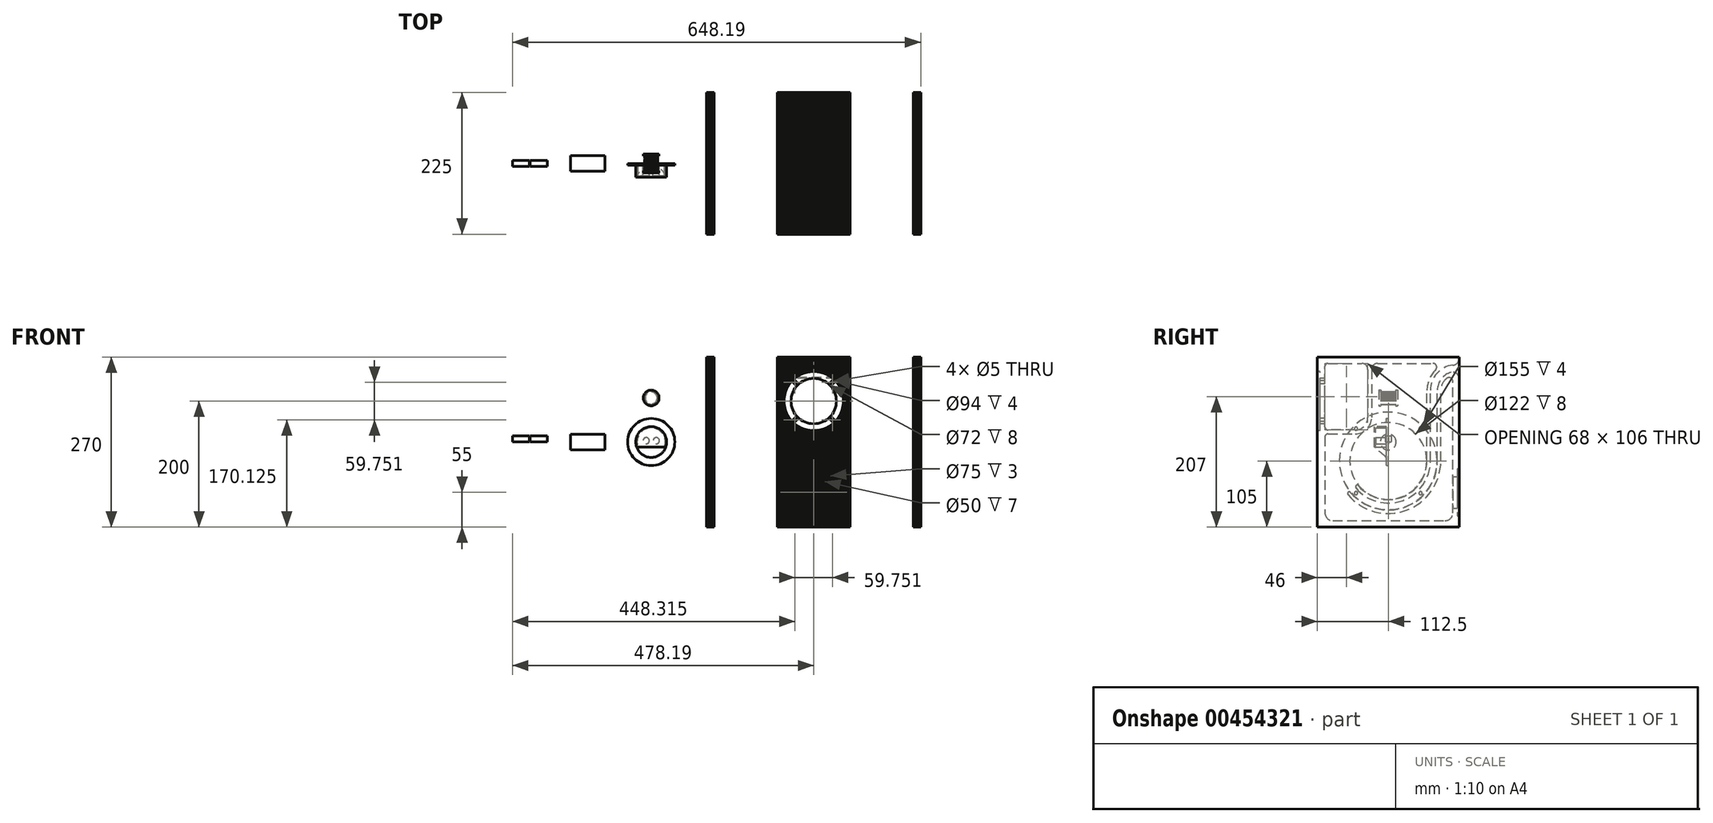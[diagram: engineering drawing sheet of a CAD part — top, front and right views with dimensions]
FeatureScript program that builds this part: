
annotation { "Feature Type Name" : "Feature", "Feature Type Description" : "" }
export const myFeature = defineFeature(function(context is Context, id is Id, definition is map)
    precondition{}
    {
        {
            var Q0;
            Q0=qCreatedBy(makeId("Right.planeOp"),FACE);
            var sketch = newSketch(context, id + "F0", { "sketchPlane" : qUnion([Q0])});
            skLineSegment(sketch, "E0", {"start": v(255.52, -132.38) * mm, "end": v(480.52, -132.38) * mm, "construction": true});
            skLineSegment(sketch, "E1", {"start": v(480.52, -132.38) * mm, "end": v(480.52, 137.62) * mm, "construction": true});
            skSolve(sketch);
        }
        {
            var Q0;
            Q0=qCreatedBy(makeId("Right.planeOp"),FACE);
            var sketch = newSketch(context, id + "F1", { "sketchPlane" : qUnion([Q0])});
            skPoint(sketch, "E2.middle", {"position": v(0, 0) * mm});
            skArc(sketch, "E3.MirrorCS", {"start": v(-88, -125) * mm, "mid": v(-96.84, -121.34) * mm, "end": v(-100.5, -112.5) * mm});
            skArc(sketch, "E4.MirrorCS", {"start": v(-95.5, 19) * mm, "mid": v(-99.04, 20.46) * mm, "end": v(-100.5, 24) * mm});
            skLineSegment(sketch, "E5", {"start": v(-100.5, 24) * mm, "end": v(-100.5, 120) * mm});
            skArc(sketch, "E6", {"start": v(-95.5, 125) * mm, "mid": v(-99.04, 123.54) * mm, "end": v(-100.5, 120) * mm});
            skLineSegment(sketch, "E7", {"start": v(-95.5, 125) * mm, "end": v(-42.5, 125) * mm});
            skArc(sketch, "E8", {"start": v(-32.5, 115) * mm, "mid": v(-35.43, 122.07) * mm, "end": v(-42.5, 125) * mm});
            skLineSegment(sketch, "E9", {"start": v(-32.5, 115) * mm, "end": v(-32.5, 39) * mm});
            skArc(sketch, "E10", {"start": v(-52.5, 19) * mm, "mid": v(-38.36, 24.86) * mm, "end": v(-32.5, 39) * mm});
            skLineSegment(sketch, "E11", {"start": v(-52.5, 19) * mm, "end": v(-95.5, 19) * mm});
            skLineSegment(sketch, "E12", {"start": v(-95.5, 13) * mm, "end": v(-52.5, 13) * mm});
            skLineSegment(sketch, "E13", {"start": v(-26.5, 115) * mm, "end": v(-26.5, 39) * mm});
            skArc(sketch, "E14", {"start": v(-52.5, 13) * mm, "mid": v(-34.12, 20.62) * mm, "end": v(-26.5, 39) * mm});
            skArc(sketch, "E15", {"start": v(-16.5, 125) * mm, "mid": v(-23.57, 122.07) * mm, "end": v(-26.5, 115) * mm});
            skArc(sketch, "E16", {"start": v(-95.5, 13) * mm, "mid": v(-99.04, 11.54) * mm, "end": v(-100.5, 8) * mm});
            skLineSegment(sketch, "E17", {"start": v(-100.5, 8) * mm, "end": v(-100.5, -112.5) * mm});
            skLineSegment(sketch, "E18", {"start": v(-88, -125) * mm, "end": v(90, -125) * mm});
            skArc(sketch, "E19", {"start": v(90, -125) * mm, "mid": v(98.84, -121.34) * mm, "end": v(102.5, -112.5) * mm});
            skLineSegment(sketch, "E20", {"start": v(102.5, -112.5) * mm, "end": v(102.5, 96.26) * mm});
            skLineSegment(sketch, "E21", {"start": v(-16.5, 125) * mm, "end": v(70.97, 125) * mm});
            skArc(sketch, "E22", {"start": v(75.35, 114.9) * mm, "mid": v(76.47, 121.39) * mm, "end": v(70.97, 125) * mm});
            skArc(sketch, "E23", {"start": v(112.5, 100.85) * mm, "mid": v(108.7, 108.7) * mm, "end": v(100.2, 110.58) * mm});
            skLineSegment(sketch, "E24", {"start": v(0, -30) * mm, "end": v(-76.6, -94.28) * mm, "construction": true});
            skArc(sketch, "E25", {"start": v(67, -30) * mm, "mid": v(22.92, -92.96) * mm, "end": v(-51.32, -73.07) * mm});
            skArc(sketch, "E26", {"start": v(102.5, 122.2) * mm, "mid": v(109.57, 125.12) * mm, "end": v(112.5, 132.2) * mm});
            skArc(sketch, "E27", {"start": v(78, -30) * mm, "mid": v(26.68, -103.3) * mm, "end": v(-59.75, -80.14) * mm});
            skArc(sketch, "E28", {"start": v(102.5, 96.26) * mm, "mid": v(99.32, 101.55) * mm, "end": v(93.16, 101.24) * mm});
            skLineSegment(sketch, "E29.bottom", {"start": v(-112.5, 135) * mm, "end": v(112.5, 135) * mm});
            skLineSegment(sketch, "E29.top", {"start": v(-112.5, -135) * mm, "end": v(112.5, -135) * mm});
            skLineSegment(sketch, "E29.left", {"start": v(-112.5, 135) * mm, "end": v(-112.5, -135) * mm});
            skLineSegment(sketch, "E30", {"start": v(112.5, 100.85) * mm, "end": v(112.5, -135) * mm});
            skArc(sketch, "E31", {"start": v(67, 82) * mm, "mid": v(77.15, 108.81) * mm, "end": v(102.5, 122.2) * mm});
            skLineSegment(sketch, "E32", {"start": v(112.5, 135) * mm, "end": v(112.5, 132.2) * mm});
            skArc(sketch, "E33", {"start": v(78, 82) * mm, "mid": v(84.2, 100.1) * mm, "end": v(100.2, 110.58) * mm});
            skArc(sketch, "E34", {"start": v(61.5, -30) * mm, "mid": v(21.03, -87.8) * mm, "end": v(-47.11, -69.53) * mm});
            skArc(sketch, "E35", {"start": v(83.5, -30) * mm, "mid": v(28.56, -108.46) * mm, "end": v(-63.96, -83.67) * mm});
            skArc(sketch, "E36", {"start": v(-59.75, -80.14) * mm, "mid": v(-63.63, -79.8) * mm, "end": v(-63.96, -83.67) * mm});
            skArc(sketch, "E37", {"start": v(-47.11, -69.53) * mm, "mid": v(-50.99, -69.2) * mm, "end": v(-51.32, -73.07) * mm});
            skLineSegment(sketch, "E38", {"start": v(67, -30) * mm, "end": v(67, 82) * mm});
            skLineSegment(sketch, "E39", {"start": v(78, -30) * mm, "end": v(78, 82) * mm});
            skLineSegment(sketch, "E40", {"start": v(61.5, -30) * mm, "end": v(61.5, 82) * mm});
            skArc(sketch, "E41", {"start": v(61.5, 82) * mm, "mid": v(65.1, 99.85) * mm, "end": v(75.35, 114.9) * mm});
            skLineSegment(sketch, "E42", {"start": v(83.5, -30) * mm, "end": v(83.5, 82) * mm});
            skArc(sketch, "E43", {"start": v(83.5, 82) * mm, "mid": v(86.05, 92.76) * mm, "end": v(93.16, 101.24) * mm});
            skSolve(sketch);
        }
        {
            var Q0;
            Q0 = qSketchRegion(id + "F1", true);
            extrude(context, id + "F2", {"entities" : qUnion([Q0]), "depth" : 116 * mm, "offsetDistance" : 25 * mm});
        }
        {
            var Q0;
            Q0=qCreatedBy(makeId("Top.planeOp"),FACE);
            var sketch = newSketch(context, id + "F3", { "sketchPlane" : qUnion([Q0])});
            skLineSegment(sketch, "E44.bottom", {"start": v(-112, 112.5) * mm, "end": v(-100, 112.5) * mm});
            skLineSegment(sketch, "E44.top", {"start": v(-112, -112.5) * mm, "end": v(-100, -112.5) * mm});
            skLineSegment(sketch, "E44.left", {"start": v(-112, 112.5) * mm, "end": v(-112, -112.5) * mm});
            skLineSegment(sketch, "E44.right", {"start": v(-100, 112.5) * mm, "end": v(-100, -112.5) * mm});
            skPoint(sketch, "E44.middle", {"position": v(-106, 0) * mm});
            skSolve(sketch);
        }
        {
            var Q0;
            Q0 = qSketchRegion(id + "F3", true);
            extrude(context, id + "F4", {"entities" : qUnion([Q0]), "depth" : 270 * mm, "offsetDistance" : 25 * mm, "symmetric" : true});
        }
        {
            var Q0;
            Q0=makeQuery(id+"F4.opExtrude","SWEPT_FACE",FACE,{"disambiguationData":[OSD([sQuery(id+"F3.wireOp",EDGE,"E44.left")])]});
            var sketch = newSketch(context, id + "F5", { "sketchPlane" : qUnion([Q0])});
            skCircle(sketch, "E45", {"center": v(0, -30) * mm, "radius": 77.5 * mm});
            skPoint(sketch, "E45.centerSnap0", {"position": v(0, -135) * mm});
            skSolve(sketch);
        }
        {
            var Q0;
            Q0 = qSketchRegion(id + "F5", true);
            extrude(context, id + "F6", {"entities" : qUnion([Q0]), "operationType" : NewBodyOperationType.REMOVE, "oppositeDirection" : true, "depth" : 4 * mm, "offsetDistance" : 25 * mm});
        }
        {
            var Q0;
            Q0=makeQuery(id+"F6.boolean.opBoolean","COPY",FACE,{"derivedFrom":makeQuery(id+"F6.opExtrude","CAP_FACE",FACE,{"disambiguationData":[OSD([sQuery(id+"F5.wireOp",EDGE,"E45")])],"isStart":false})});
            var sketch = newSketch(context, id + "F7", { "sketchPlane" : qUnion([Q0])});
            skCircle(sketch, "E46", {"center": v(0, -30) * mm, "radius": 61 * mm});
            skSolve(sketch);
        }
        {
            var Q0;
            Q0 = qSketchRegion(id + "F7", true);
            extrude(context, id + "F8", {"entities" : qUnion([Q0]), "operationType" : NewBodyOperationType.REMOVE, "oppositeDirection" : true, "depth" : 8 * mm, "offsetDistance" : 25 * mm});
        }
        {
            var Q0;
            Q0=qCreatedBy(makeId("Top.planeOp"),FACE);
            var sketch = newSketch(context, id + "F9", { "sketchPlane" : qUnion([Q0])});
            skLineSegment(sketch, "E47.bottom", {"start": v(228, 112.5) * mm, "end": v(216, 112.5) * mm});
            skLineSegment(sketch, "E47.top", {"start": v(228, -112.5) * mm, "end": v(216, -112.5) * mm});
            skLineSegment(sketch, "E47.left", {"start": v(228, 112.5) * mm, "end": v(228, -112.5) * mm});
            skLineSegment(sketch, "E47.right", {"start": v(216, 112.5) * mm, "end": v(216, -112.5) * mm});
            skPoint(sketch, "E47.middle", {"position": v(222, 0) * mm});
            skSolve(sketch);
        }
        {
            var Q0;
            Q0 = qSketchRegion(id + "F9", true);
            extrude(context, id + "F10", {"entities" : qUnion([Q0]), "depth" : 270 * mm, "offsetDistance" : 25 * mm, "symmetric" : true});
        }
        {
            var Q0;
            Q0=makeQuery(id+"F2.opExtrude","SWEPT_FACE",FACE,{"disambiguationData":[OSD([sQuery(id+"F1.wireOp",EDGE,"E29.left")])]});
            var sketch = newSketch(context, id + "F11", { "sketchPlane" : qUnion([Q0])});
            skCircle(sketch, "E48", {"center": v(58, 65) * mm, "radius": 47 * mm});
            skPoint(sketch, "E48.centerSnap0", {"position": v(58, 135) * mm});
            skSolve(sketch);
        }
        {
            var Q0;
            Q0 = qSketchRegion(id + "F11", true);
            extrude(context, id + "F12", {"entities" : qUnion([Q0]), "operationType" : NewBodyOperationType.REMOVE, "oppositeDirection" : true, "depth" : 4 * mm, "offsetDistance" : 25 * mm});
        }
        {
            var Q0;
            Q0=makeQuery(id+"F12.boolean.opBoolean","COPY",FACE,{"derivedFrom":makeQuery(id+"F12.opExtrude","CAP_FACE",FACE,{"disambiguationData":[OSD([sQuery(id+"F11.wireOp",EDGE,"E48")])],"isStart":false})});
            var sketch = newSketch(context, id + "F13", { "sketchPlane" : qUnion([Q0])});
            skCircle(sketch, "E49", {"center": v(58, 65) * mm, "radius": 36 * mm});
            skSolve(sketch);
        }
        {
            var Q0;
            Q0 = qSketchRegion(id + "F13", true);
            extrude(context, id + "F14", {"entities" : qUnion([Q0]), "operationType" : NewBodyOperationType.REMOVE, "oppositeDirection" : true, "depth" : 8 * mm, "offsetDistance" : 25 * mm});
        }
        {
            var Q0;
            Q0=makeQuery(id+"F2.opExtrude","SWEPT_FACE",FACE,{"disambiguationData":[OSD([sQuery(id+"F1.wireOp",EDGE,"E29.left")])]});
            var sketch = newSketch(context, id + "F15", { "sketchPlane" : qUnion([Q0])});
            skLineSegment(sketch, "E50.bottom", {"start": v(224, -150) * mm, "end": v(226, -150) * mm});
            skLineSegment(sketch, "E50.top", {"start": v(224, 150) * mm, "end": v(226, 150) * mm});
            skLineSegment(sketch, "E50.left", {"start": v(224, -150) * mm, "end": v(224, 150) * mm});
            skLineSegment(sketch, "E50.right", {"start": v(226, -150) * mm, "end": v(226, 150) * mm});
            skPoint(sketch, "E50.middle", {"position": v(225, 0) * mm});
            skLineSegment(sketch, "E51.1.0.0", {"start": v(220, 150) * mm, "end": v(222, 150) * mm});
            skLineSegment(sketch, "E51.1.0.1", {"start": v(220, -150) * mm, "end": v(220, 150) * mm});
            skLineSegment(sketch, "E51.1.0.2", {"start": v(222, -150) * mm, "end": v(222, 150) * mm});
            skLineSegment(sketch, "E51.1.0.3", {"start": v(220, -150) * mm, "end": v(222, -150) * mm});
            skLineSegment(sketch, "E51.2.0.0", {"start": v(216, 150) * mm, "end": v(218, 150) * mm});
            skLineSegment(sketch, "E51.2.0.1", {"start": v(216, -150) * mm, "end": v(216, 150) * mm});
            skLineSegment(sketch, "E51.2.0.2", {"start": v(218, -150) * mm, "end": v(218, 150) * mm});
            skLineSegment(sketch, "E51.2.0.3", {"start": v(216, -150) * mm, "end": v(218, -150) * mm});
            skLineSegment(sketch, "E51.3.0.0", {"start": v(212, 150) * mm, "end": v(214, 150) * mm});
            skLineSegment(sketch, "E51.3.0.1", {"start": v(212, -150) * mm, "end": v(212, 150) * mm});
            skLineSegment(sketch, "E51.3.0.2", {"start": v(214, -150) * mm, "end": v(214, 150) * mm});
            skLineSegment(sketch, "E51.3.0.3", {"start": v(212, -150) * mm, "end": v(214, -150) * mm});
            skLineSegment(sketch, "E51.4.0.0", {"start": v(208, 150) * mm, "end": v(210, 150) * mm});
            skLineSegment(sketch, "E51.4.0.1", {"start": v(208, -150) * mm, "end": v(208, 150) * mm});
            skLineSegment(sketch, "E51.4.0.2", {"start": v(210, -150) * mm, "end": v(210, 150) * mm});
            skLineSegment(sketch, "E51.4.0.3", {"start": v(208, -150) * mm, "end": v(210, -150) * mm});
            skLineSegment(sketch, "E51.5.0.0", {"start": v(204, 150) * mm, "end": v(206, 150) * mm});
            skLineSegment(sketch, "E51.5.0.1", {"start": v(204, -150) * mm, "end": v(204, 150) * mm});
            skLineSegment(sketch, "E51.5.0.2", {"start": v(206, -150) * mm, "end": v(206, 150) * mm});
            skLineSegment(sketch, "E51.5.0.3", {"start": v(204, -150) * mm, "end": v(206, -150) * mm});
            skLineSegment(sketch, "E51.6.0.0", {"start": v(200, 150) * mm, "end": v(202, 150) * mm});
            skLineSegment(sketch, "E51.6.0.1", {"start": v(200, -150) * mm, "end": v(200, 150) * mm});
            skLineSegment(sketch, "E51.6.0.2", {"start": v(202, -150) * mm, "end": v(202, 150) * mm});
            skLineSegment(sketch, "E51.6.0.3", {"start": v(200, -150) * mm, "end": v(202, -150) * mm});
            skLineSegment(sketch, "E51.7.0.0", {"start": v(196, 150) * mm, "end": v(198, 150) * mm});
            skLineSegment(sketch, "E51.7.0.1", {"start": v(196, -150) * mm, "end": v(196, 150) * mm});
            skLineSegment(sketch, "E51.7.0.2", {"start": v(198, -150) * mm, "end": v(198, 150) * mm});
            skLineSegment(sketch, "E51.7.0.3", {"start": v(196, -150) * mm, "end": v(198, -150) * mm});
            skLineSegment(sketch, "E51.8.0.0", {"start": v(192, 150) * mm, "end": v(194, 150) * mm});
            skLineSegment(sketch, "E51.8.0.1", {"start": v(192, -150) * mm, "end": v(192, 150) * mm});
            skLineSegment(sketch, "E51.8.0.2", {"start": v(194, -150) * mm, "end": v(194, 150) * mm});
            skLineSegment(sketch, "E51.8.0.3", {"start": v(192, -150) * mm, "end": v(194, -150) * mm});
            skLineSegment(sketch, "E51.9.0.0", {"start": v(188, 150) * mm, "end": v(190, 150) * mm});
            skLineSegment(sketch, "E51.9.0.1", {"start": v(188, -150) * mm, "end": v(188, 150) * mm});
            skLineSegment(sketch, "E51.9.0.2", {"start": v(190, -150) * mm, "end": v(190, 150) * mm});
            skLineSegment(sketch, "E51.9.0.3", {"start": v(188, -150) * mm, "end": v(190, -150) * mm});
            skLineSegment(sketch, "E51.10.0.0", {"start": v(184, 150) * mm, "end": v(186, 150) * mm});
            skLineSegment(sketch, "E51.10.0.1", {"start": v(184, -150) * mm, "end": v(184, 150) * mm});
            skLineSegment(sketch, "E51.10.0.2", {"start": v(186, -150) * mm, "end": v(186, 150) * mm});
            skLineSegment(sketch, "E51.10.0.3", {"start": v(184, -150) * mm, "end": v(186, -150) * mm});
            skLineSegment(sketch, "E51.11.0.0", {"start": v(180, 150) * mm, "end": v(182, 150) * mm});
            skLineSegment(sketch, "E51.11.0.1", {"start": v(180, -150) * mm, "end": v(180, 150) * mm});
            skLineSegment(sketch, "E51.11.0.2", {"start": v(182, -150) * mm, "end": v(182, 150) * mm});
            skLineSegment(sketch, "E51.11.0.3", {"start": v(180, -150) * mm, "end": v(182, -150) * mm});
            skLineSegment(sketch, "E51.12.0.0", {"start": v(176, 150) * mm, "end": v(178, 150) * mm});
            skLineSegment(sketch, "E51.12.0.1", {"start": v(176, -150) * mm, "end": v(176, 150) * mm});
            skLineSegment(sketch, "E51.12.0.2", {"start": v(178, -150) * mm, "end": v(178, 150) * mm});
            skLineSegment(sketch, "E51.12.0.3", {"start": v(176, -150) * mm, "end": v(178, -150) * mm});
            skLineSegment(sketch, "E51.13.0.0", {"start": v(172, 150) * mm, "end": v(174, 150) * mm});
            skLineSegment(sketch, "E51.13.0.1", {"start": v(172, -150) * mm, "end": v(172, 150) * mm});
            skLineSegment(sketch, "E51.13.0.2", {"start": v(174, -150) * mm, "end": v(174, 150) * mm});
            skLineSegment(sketch, "E51.13.0.3", {"start": v(172, -150) * mm, "end": v(174, -150) * mm});
            skLineSegment(sketch, "E51.14.0.0", {"start": v(168, 150) * mm, "end": v(170, 150) * mm});
            skLineSegment(sketch, "E51.14.0.1", {"start": v(168, -150) * mm, "end": v(168, 150) * mm});
            skLineSegment(sketch, "E51.14.0.2", {"start": v(170, -150) * mm, "end": v(170, 150) * mm});
            skLineSegment(sketch, "E51.14.0.3", {"start": v(168, -150) * mm, "end": v(170, -150) * mm});
            skLineSegment(sketch, "E51.15.0.0", {"start": v(164, 150) * mm, "end": v(166, 150) * mm});
            skLineSegment(sketch, "E51.15.0.1", {"start": v(164, -150) * mm, "end": v(164, 150) * mm});
            skLineSegment(sketch, "E51.15.0.2", {"start": v(166, -150) * mm, "end": v(166, 150) * mm});
            skLineSegment(sketch, "E51.15.0.3", {"start": v(164, -150) * mm, "end": v(166, -150) * mm});
            skLineSegment(sketch, "E51.16.0.0", {"start": v(160, 150) * mm, "end": v(162, 150) * mm});
            skLineSegment(sketch, "E51.16.0.1", {"start": v(160, -150) * mm, "end": v(160, 150) * mm});
            skLineSegment(sketch, "E51.16.0.2", {"start": v(162, -150) * mm, "end": v(162, 150) * mm});
            skLineSegment(sketch, "E51.16.0.3", {"start": v(160, -150) * mm, "end": v(162, -150) * mm});
            skLineSegment(sketch, "E51.17.0.0", {"start": v(156, 150) * mm, "end": v(158, 150) * mm});
            skLineSegment(sketch, "E51.17.0.1", {"start": v(156, -150) * mm, "end": v(156, 150) * mm});
            skLineSegment(sketch, "E51.17.0.2", {"start": v(158, -150) * mm, "end": v(158, 150) * mm});
            skLineSegment(sketch, "E51.17.0.3", {"start": v(156, -150) * mm, "end": v(158, -150) * mm});
            skLineSegment(sketch, "E51.18.0.0", {"start": v(152, 150) * mm, "end": v(154, 150) * mm});
            skLineSegment(sketch, "E51.18.0.1", {"start": v(152, -150) * mm, "end": v(152, 150) * mm});
            skLineSegment(sketch, "E51.18.0.2", {"start": v(154, -150) * mm, "end": v(154, 150) * mm});
            skLineSegment(sketch, "E51.18.0.3", {"start": v(152, -150) * mm, "end": v(154, -150) * mm});
            skLineSegment(sketch, "E51.19.0.0", {"start": v(148, 150) * mm, "end": v(150, 150) * mm});
            skLineSegment(sketch, "E51.19.0.1", {"start": v(148, -150) * mm, "end": v(148, 150) * mm});
            skLineSegment(sketch, "E51.19.0.2", {"start": v(150, -150) * mm, "end": v(150, 150) * mm});
            skLineSegment(sketch, "E51.19.0.3", {"start": v(148, -150) * mm, "end": v(150, -150) * mm});
            skLineSegment(sketch, "E51.20.0.0", {"start": v(144, 150) * mm, "end": v(146, 150) * mm});
            skLineSegment(sketch, "E51.20.0.1", {"start": v(144, -150) * mm, "end": v(144, 150) * mm});
            skLineSegment(sketch, "E51.20.0.2", {"start": v(146, -150) * mm, "end": v(146, 150) * mm});
            skLineSegment(sketch, "E51.20.0.3", {"start": v(144, -150) * mm, "end": v(146, -150) * mm});
            skLineSegment(sketch, "E51.21.0.0", {"start": v(140, 150) * mm, "end": v(142, 150) * mm});
            skLineSegment(sketch, "E51.21.0.1", {"start": v(140, -150) * mm, "end": v(140, 150) * mm});
            skLineSegment(sketch, "E51.21.0.2", {"start": v(142, -150) * mm, "end": v(142, 150) * mm});
            skLineSegment(sketch, "E51.21.0.3", {"start": v(140, -150) * mm, "end": v(142, -150) * mm});
            skLineSegment(sketch, "E51.22.0.0", {"start": v(136, 150) * mm, "end": v(138, 150) * mm});
            skLineSegment(sketch, "E51.22.0.1", {"start": v(136, -150) * mm, "end": v(136, 150) * mm});
            skLineSegment(sketch, "E51.22.0.2", {"start": v(138, -150) * mm, "end": v(138, 150) * mm});
            skLineSegment(sketch, "E51.22.0.3", {"start": v(136, -150) * mm, "end": v(138, -150) * mm});
            skLineSegment(sketch, "E51.23.0.0", {"start": v(132, 150) * mm, "end": v(134, 150) * mm});
            skLineSegment(sketch, "E51.23.0.1", {"start": v(132, -150) * mm, "end": v(132, 150) * mm});
            skLineSegment(sketch, "E51.23.0.2", {"start": v(134, -150) * mm, "end": v(134, 150) * mm});
            skLineSegment(sketch, "E51.23.0.3", {"start": v(132, -150) * mm, "end": v(134, -150) * mm});
            skLineSegment(sketch, "E51.24.0.0", {"start": v(128, 150) * mm, "end": v(130, 150) * mm});
            skLineSegment(sketch, "E51.24.0.1", {"start": v(128, -150) * mm, "end": v(128, 150) * mm});
            skLineSegment(sketch, "E51.24.0.2", {"start": v(130, -150) * mm, "end": v(130, 150) * mm});
            skLineSegment(sketch, "E51.24.0.3", {"start": v(128, -150) * mm, "end": v(130, -150) * mm});
            skLineSegment(sketch, "E51.25.0.0", {"start": v(124, 150) * mm, "end": v(126, 150) * mm});
            skLineSegment(sketch, "E51.25.0.1", {"start": v(124, -150) * mm, "end": v(124, 150) * mm});
            skLineSegment(sketch, "E51.25.0.2", {"start": v(126, -150) * mm, "end": v(126, 150) * mm});
            skLineSegment(sketch, "E51.25.0.3", {"start": v(124, -150) * mm, "end": v(126, -150) * mm});
            skLineSegment(sketch, "E51.26.0.0", {"start": v(120, 150) * mm, "end": v(122, 150) * mm});
            skLineSegment(sketch, "E51.26.0.1", {"start": v(120, -150) * mm, "end": v(120, 150) * mm});
            skLineSegment(sketch, "E51.26.0.2", {"start": v(122, -150) * mm, "end": v(122, 150) * mm});
            skLineSegment(sketch, "E51.26.0.3", {"start": v(120, -150) * mm, "end": v(122, -150) * mm});
            skLineSegment(sketch, "E51.27.0.0", {"start": v(116, 150) * mm, "end": v(118, 150) * mm});
            skLineSegment(sketch, "E51.27.0.1", {"start": v(116, -150) * mm, "end": v(116, 150) * mm});
            skLineSegment(sketch, "E51.27.0.2", {"start": v(118, -150) * mm, "end": v(118, 150) * mm});
            skLineSegment(sketch, "E51.27.0.3", {"start": v(116, -150) * mm, "end": v(118, -150) * mm});
            skLineSegment(sketch, "E51.28.0.0", {"start": v(112, 150) * mm, "end": v(114, 150) * mm});
            skLineSegment(sketch, "E51.28.0.1", {"start": v(112, -150) * mm, "end": v(112, 150) * mm});
            skLineSegment(sketch, "E51.28.0.2", {"start": v(114, -150) * mm, "end": v(114, 150) * mm});
            skLineSegment(sketch, "E51.28.0.3", {"start": v(112, -150) * mm, "end": v(114, -150) * mm});
            skLineSegment(sketch, "E51.29.0.0", {"start": v(108, 150) * mm, "end": v(110, 150) * mm});
            skLineSegment(sketch, "E51.29.0.1", {"start": v(108, -150) * mm, "end": v(108, 150) * mm});
            skLineSegment(sketch, "E51.29.0.2", {"start": v(110, -150) * mm, "end": v(110, 150) * mm});
            skLineSegment(sketch, "E51.29.0.3", {"start": v(108, -150) * mm, "end": v(110, -150) * mm});
            skLineSegment(sketch, "E51.30.0.0", {"start": v(104, 150) * mm, "end": v(106, 150) * mm});
            skLineSegment(sketch, "E51.30.0.1", {"start": v(104, -150) * mm, "end": v(104, 150) * mm});
            skLineSegment(sketch, "E51.30.0.2", {"start": v(106, -150) * mm, "end": v(106, 150) * mm});
            skLineSegment(sketch, "E51.30.0.3", {"start": v(104, -150) * mm, "end": v(106, -150) * mm});
            skLineSegment(sketch, "E51.31.0.0", {"start": v(100, 150) * mm, "end": v(102, 150) * mm});
            skLineSegment(sketch, "E51.31.0.1", {"start": v(100, -150) * mm, "end": v(100, 150) * mm});
            skLineSegment(sketch, "E51.31.0.2", {"start": v(102, -150) * mm, "end": v(102, 150) * mm});
            skLineSegment(sketch, "E51.31.0.3", {"start": v(100, -150) * mm, "end": v(102, -150) * mm});
            skLineSegment(sketch, "E51.32.0.0", {"start": v(96, 150) * mm, "end": v(98, 150) * mm});
            skLineSegment(sketch, "E51.32.0.1", {"start": v(96, -150) * mm, "end": v(96, 150) * mm});
            skLineSegment(sketch, "E51.32.0.2", {"start": v(98, -150) * mm, "end": v(98, 150) * mm});
            skLineSegment(sketch, "E51.32.0.3", {"start": v(96, -150) * mm, "end": v(98, -150) * mm});
            skLineSegment(sketch, "E51.33.0.0", {"start": v(92, 150) * mm, "end": v(94, 150) * mm});
            skLineSegment(sketch, "E51.33.0.1", {"start": v(92, -150) * mm, "end": v(92, 150) * mm});
            skLineSegment(sketch, "E51.33.0.2", {"start": v(94, -150) * mm, "end": v(94, 150) * mm});
            skLineSegment(sketch, "E51.33.0.3", {"start": v(92, -150) * mm, "end": v(94, -150) * mm});
            skLineSegment(sketch, "E51.34.0.0", {"start": v(88, 150) * mm, "end": v(90, 150) * mm});
            skLineSegment(sketch, "E51.34.0.1", {"start": v(88, -150) * mm, "end": v(88, 150) * mm});
            skLineSegment(sketch, "E51.34.0.2", {"start": v(90, -150) * mm, "end": v(90, 150) * mm});
            skLineSegment(sketch, "E51.34.0.3", {"start": v(88, -150) * mm, "end": v(90, -150) * mm});
            skLineSegment(sketch, "E51.35.0.0", {"start": v(84, 150) * mm, "end": v(86, 150) * mm});
            skLineSegment(sketch, "E51.35.0.1", {"start": v(84, -150) * mm, "end": v(84, 150) * mm});
            skLineSegment(sketch, "E51.35.0.2", {"start": v(86, -150) * mm, "end": v(86, 150) * mm});
            skLineSegment(sketch, "E51.35.0.3", {"start": v(84, -150) * mm, "end": v(86, -150) * mm});
            skLineSegment(sketch, "E51.36.0.0", {"start": v(80, 150) * mm, "end": v(82, 150) * mm});
            skLineSegment(sketch, "E51.36.0.1", {"start": v(80, -150) * mm, "end": v(80, 150) * mm});
            skLineSegment(sketch, "E51.36.0.2", {"start": v(82, -150) * mm, "end": v(82, 150) * mm});
            skLineSegment(sketch, "E51.36.0.3", {"start": v(80, -150) * mm, "end": v(82, -150) * mm});
            skLineSegment(sketch, "E51.37.0.0", {"start": v(76, 150) * mm, "end": v(78, 150) * mm});
            skLineSegment(sketch, "E51.37.0.1", {"start": v(76, -150) * mm, "end": v(76, 150) * mm});
            skLineSegment(sketch, "E51.37.0.2", {"start": v(78, -150) * mm, "end": v(78, 150) * mm});
            skLineSegment(sketch, "E51.37.0.3", {"start": v(76, -150) * mm, "end": v(78, -150) * mm});
            skLineSegment(sketch, "E51.38.0.0", {"start": v(72, 150) * mm, "end": v(74, 150) * mm});
            skLineSegment(sketch, "E51.38.0.1", {"start": v(72, -150) * mm, "end": v(72, 150) * mm});
            skLineSegment(sketch, "E51.38.0.2", {"start": v(74, -150) * mm, "end": v(74, 150) * mm});
            skLineSegment(sketch, "E51.38.0.3", {"start": v(72, -150) * mm, "end": v(74, -150) * mm});
            skLineSegment(sketch, "E51.39.0.0", {"start": v(68, 150) * mm, "end": v(70, 150) * mm});
            skLineSegment(sketch, "E51.39.0.1", {"start": v(68, -150) * mm, "end": v(68, 150) * mm});
            skLineSegment(sketch, "E51.39.0.2", {"start": v(70, -150) * mm, "end": v(70, 150) * mm});
            skLineSegment(sketch, "E51.39.0.3", {"start": v(68, -150) * mm, "end": v(70, -150) * mm});
            skLineSegment(sketch, "E51.40.0.0", {"start": v(64, 150) * mm, "end": v(66, 150) * mm});
            skLineSegment(sketch, "E51.40.0.1", {"start": v(64, -150) * mm, "end": v(64, 150) * mm});
            skLineSegment(sketch, "E51.40.0.2", {"start": v(66, -150) * mm, "end": v(66, 150) * mm});
            skLineSegment(sketch, "E51.40.0.3", {"start": v(64, -150) * mm, "end": v(66, -150) * mm});
            skLineSegment(sketch, "E51.41.0.0", {"start": v(60, 150) * mm, "end": v(62, 150) * mm});
            skLineSegment(sketch, "E51.41.0.1", {"start": v(60, -150) * mm, "end": v(60, 150) * mm});
            skLineSegment(sketch, "E51.41.0.2", {"start": v(62, -150) * mm, "end": v(62, 150) * mm});
            skLineSegment(sketch, "E51.41.0.3", {"start": v(60, -150) * mm, "end": v(62, -150) * mm});
            skLineSegment(sketch, "E51.42.0.0", {"start": v(56, 150) * mm, "end": v(58, 150) * mm});
            skLineSegment(sketch, "E51.42.0.1", {"start": v(56, -150) * mm, "end": v(56, 150) * mm});
            skLineSegment(sketch, "E51.42.0.2", {"start": v(58, -150) * mm, "end": v(58, 150) * mm});
            skLineSegment(sketch, "E51.42.0.3", {"start": v(56, -150) * mm, "end": v(58, -150) * mm});
            skLineSegment(sketch, "E51.43.0.0", {"start": v(52, 150) * mm, "end": v(54, 150) * mm});
            skLineSegment(sketch, "E51.43.0.1", {"start": v(52, -150) * mm, "end": v(52, 150) * mm});
            skLineSegment(sketch, "E51.43.0.2", {"start": v(54, -150) * mm, "end": v(54, 150) * mm});
            skLineSegment(sketch, "E51.43.0.3", {"start": v(52, -150) * mm, "end": v(54, -150) * mm});
            skLineSegment(sketch, "E51.44.0.0", {"start": v(48, 150) * mm, "end": v(50, 150) * mm});
            skLineSegment(sketch, "E51.44.0.1", {"start": v(48, -150) * mm, "end": v(48, 150) * mm});
            skLineSegment(sketch, "E51.44.0.2", {"start": v(50, -150) * mm, "end": v(50, 150) * mm});
            skLineSegment(sketch, "E51.44.0.3", {"start": v(48, -150) * mm, "end": v(50, -150) * mm});
            skLineSegment(sketch, "E51.45.0.0", {"start": v(44, 150) * mm, "end": v(46, 150) * mm});
            skLineSegment(sketch, "E51.45.0.1", {"start": v(44, -150) * mm, "end": v(44, 150) * mm});
            skLineSegment(sketch, "E51.45.0.2", {"start": v(46, -150) * mm, "end": v(46, 150) * mm});
            skLineSegment(sketch, "E51.45.0.3", {"start": v(44, -150) * mm, "end": v(46, -150) * mm});
            skLineSegment(sketch, "E51.46.0.0", {"start": v(40, 150) * mm, "end": v(42, 150) * mm});
            skLineSegment(sketch, "E51.46.0.1", {"start": v(40, -150) * mm, "end": v(40, 150) * mm});
            skLineSegment(sketch, "E51.46.0.2", {"start": v(42, -150) * mm, "end": v(42, 150) * mm});
            skLineSegment(sketch, "E51.46.0.3", {"start": v(40, -150) * mm, "end": v(42, -150) * mm});
            skLineSegment(sketch, "E51.47.0.0", {"start": v(36, 150) * mm, "end": v(38, 150) * mm});
            skLineSegment(sketch, "E51.47.0.1", {"start": v(36, -150) * mm, "end": v(36, 150) * mm});
            skLineSegment(sketch, "E51.47.0.2", {"start": v(38, -150) * mm, "end": v(38, 150) * mm});
            skLineSegment(sketch, "E51.47.0.3", {"start": v(36, -150) * mm, "end": v(38, -150) * mm});
            skLineSegment(sketch, "E51.48.0.0", {"start": v(32, 150) * mm, "end": v(34, 150) * mm});
            skLineSegment(sketch, "E51.48.0.1", {"start": v(32, -150) * mm, "end": v(32, 150) * mm});
            skLineSegment(sketch, "E51.48.0.2", {"start": v(34, -150) * mm, "end": v(34, 150) * mm});
            skLineSegment(sketch, "E51.48.0.3", {"start": v(32, -150) * mm, "end": v(34, -150) * mm});
            skLineSegment(sketch, "E51.49.0.0", {"start": v(28, 150) * mm, "end": v(30, 150) * mm});
            skLineSegment(sketch, "E51.49.0.1", {"start": v(28, -150) * mm, "end": v(28, 150) * mm});
            skLineSegment(sketch, "E51.49.0.2", {"start": v(30, -150) * mm, "end": v(30, 150) * mm});
            skLineSegment(sketch, "E51.49.0.3", {"start": v(28, -150) * mm, "end": v(30, -150) * mm});
            skLineSegment(sketch, "E51.50.0.0", {"start": v(24, 150) * mm, "end": v(26, 150) * mm});
            skLineSegment(sketch, "E51.50.0.1", {"start": v(24, -150) * mm, "end": v(24, 150) * mm});
            skLineSegment(sketch, "E51.50.0.2", {"start": v(26, -150) * mm, "end": v(26, 150) * mm});
            skLineSegment(sketch, "E51.50.0.3", {"start": v(24, -150) * mm, "end": v(26, -150) * mm});
            skLineSegment(sketch, "E51.51.0.0", {"start": v(20, 150) * mm, "end": v(22, 150) * mm});
            skLineSegment(sketch, "E51.51.0.1", {"start": v(20, -150) * mm, "end": v(20, 150) * mm});
            skLineSegment(sketch, "E51.51.0.2", {"start": v(22, -150) * mm, "end": v(22, 150) * mm});
            skLineSegment(sketch, "E51.51.0.3", {"start": v(20, -150) * mm, "end": v(22, -150) * mm});
            skLineSegment(sketch, "E51.52.0.0", {"start": v(16, 150) * mm, "end": v(18, 150) * mm});
            skLineSegment(sketch, "E51.52.0.1", {"start": v(16, -150) * mm, "end": v(16, 150) * mm});
            skLineSegment(sketch, "E51.52.0.2", {"start": v(18, -150) * mm, "end": v(18, 150) * mm});
            skLineSegment(sketch, "E51.52.0.3", {"start": v(16, -150) * mm, "end": v(18, -150) * mm});
            skLineSegment(sketch, "E51.53.0.0", {"start": v(12, 150) * mm, "end": v(14, 150) * mm});
            skLineSegment(sketch, "E51.53.0.1", {"start": v(12, -150) * mm, "end": v(12, 150) * mm});
            skLineSegment(sketch, "E51.53.0.2", {"start": v(14, -150) * mm, "end": v(14, 150) * mm});
            skLineSegment(sketch, "E51.53.0.3", {"start": v(12, -150) * mm, "end": v(14, -150) * mm});
            skLineSegment(sketch, "E51.54.0.0", {"start": v(8, 150) * mm, "end": v(10, 150) * mm});
            skLineSegment(sketch, "E51.54.0.1", {"start": v(8, -150) * mm, "end": v(8, 150) * mm});
            skLineSegment(sketch, "E51.54.0.2", {"start": v(10, -150) * mm, "end": v(10, 150) * mm});
            skLineSegment(sketch, "E51.54.0.3", {"start": v(8, -150) * mm, "end": v(10, -150) * mm});
            skLineSegment(sketch, "E51.55.0.0", {"start": v(4, 150) * mm, "end": v(6, 150) * mm});
            skLineSegment(sketch, "E51.55.0.1", {"start": v(4, -150) * mm, "end": v(4, 150) * mm});
            skLineSegment(sketch, "E51.55.0.2", {"start": v(6, -150) * mm, "end": v(6, 150) * mm});
            skLineSegment(sketch, "E51.55.0.3", {"start": v(4, -150) * mm, "end": v(6, -150) * mm});
            skLineSegment(sketch, "E51.56.0.0", {"start": v(0, 150) * mm, "end": v(2, 150) * mm});
            skLineSegment(sketch, "E51.56.0.1", {"start": v(0, -150) * mm, "end": v(0, 150) * mm});
            skLineSegment(sketch, "E51.56.0.2", {"start": v(2, -150) * mm, "end": v(2, 150) * mm});
            skLineSegment(sketch, "E51.56.0.3", {"start": v(0, -150) * mm, "end": v(2, -150) * mm});
            skLineSegment(sketch, "E51.57.0.0", {"start": v(-4, 150) * mm, "end": v(-2, 150) * mm});
            skLineSegment(sketch, "E51.57.0.1", {"start": v(-4, -150) * mm, "end": v(-4, 150) * mm});
            skLineSegment(sketch, "E51.57.0.2", {"start": v(-2, -150) * mm, "end": v(-2, 150) * mm});
            skLineSegment(sketch, "E51.57.0.3", {"start": v(-4, -150) * mm, "end": v(-2, -150) * mm});
            skLineSegment(sketch, "E51.58.0.0", {"start": v(-8, 150) * mm, "end": v(-6, 150) * mm});
            skLineSegment(sketch, "E51.58.0.1", {"start": v(-8, -150) * mm, "end": v(-8, 150) * mm});
            skLineSegment(sketch, "E51.58.0.2", {"start": v(-6, -150) * mm, "end": v(-6, 150) * mm});
            skLineSegment(sketch, "E51.58.0.3", {"start": v(-8, -150) * mm, "end": v(-6, -150) * mm});
            skLineSegment(sketch, "E51.59.0.0", {"start": v(-12, 150) * mm, "end": v(-10, 150) * mm});
            skLineSegment(sketch, "E51.59.0.1", {"start": v(-12, -150) * mm, "end": v(-12, 150) * mm});
            skLineSegment(sketch, "E51.59.0.2", {"start": v(-10, -150) * mm, "end": v(-10, 150) * mm});
            skLineSegment(sketch, "E51.59.0.3", {"start": v(-12, -150) * mm, "end": v(-10, -150) * mm});
            skLineSegment(sketch, "E51.60.0.0", {"start": v(-16, 150) * mm, "end": v(-14, 150) * mm});
            skLineSegment(sketch, "E51.60.0.1", {"start": v(-16, -150) * mm, "end": v(-16, 150) * mm});
            skLineSegment(sketch, "E51.60.0.2", {"start": v(-14, -150) * mm, "end": v(-14, 150) * mm});
            skLineSegment(sketch, "E51.60.0.3", {"start": v(-16, -150) * mm, "end": v(-14, -150) * mm});
            skLineSegment(sketch, "E51.61.0.0", {"start": v(-20, 150) * mm, "end": v(-18, 150) * mm});
            skLineSegment(sketch, "E51.61.0.1", {"start": v(-20, -150) * mm, "end": v(-20, 150) * mm});
            skLineSegment(sketch, "E51.61.0.2", {"start": v(-18, -150) * mm, "end": v(-18, 150) * mm});
            skLineSegment(sketch, "E51.61.0.3", {"start": v(-20, -150) * mm, "end": v(-18, -150) * mm});
            skLineSegment(sketch, "E51.62.0.0", {"start": v(-24, 150) * mm, "end": v(-22, 150) * mm});
            skLineSegment(sketch, "E51.62.0.1", {"start": v(-24, -150) * mm, "end": v(-24, 150) * mm});
            skLineSegment(sketch, "E51.62.0.2", {"start": v(-22, -150) * mm, "end": v(-22, 150) * mm});
            skLineSegment(sketch, "E51.62.0.3", {"start": v(-24, -150) * mm, "end": v(-22, -150) * mm});
            skLineSegment(sketch, "E51.63.0.0", {"start": v(-28, 150) * mm, "end": v(-26, 150) * mm});
            skLineSegment(sketch, "E51.63.0.1", {"start": v(-28, -150) * mm, "end": v(-28, 150) * mm});
            skLineSegment(sketch, "E51.63.0.2", {"start": v(-26, -150) * mm, "end": v(-26, 150) * mm});
            skLineSegment(sketch, "E51.63.0.3", {"start": v(-28, -150) * mm, "end": v(-26, -150) * mm});
            skLineSegment(sketch, "E51.64.0.0", {"start": v(-32, 150) * mm, "end": v(-30, 150) * mm});
            skLineSegment(sketch, "E51.64.0.1", {"start": v(-32, -150) * mm, "end": v(-32, 150) * mm});
            skLineSegment(sketch, "E51.64.0.2", {"start": v(-30, -150) * mm, "end": v(-30, 150) * mm});
            skLineSegment(sketch, "E51.64.0.3", {"start": v(-32, -150) * mm, "end": v(-30, -150) * mm});
            skLineSegment(sketch, "E51.65.0.0", {"start": v(-36, 150) * mm, "end": v(-34, 150) * mm});
            skLineSegment(sketch, "E51.65.0.1", {"start": v(-36, -150) * mm, "end": v(-36, 150) * mm});
            skLineSegment(sketch, "E51.65.0.2", {"start": v(-34, -150) * mm, "end": v(-34, 150) * mm});
            skLineSegment(sketch, "E51.65.0.3", {"start": v(-36, -150) * mm, "end": v(-34, -150) * mm});
            skLineSegment(sketch, "E51.66.0.0", {"start": v(-40, 150) * mm, "end": v(-38, 150) * mm});
            skLineSegment(sketch, "E51.66.0.1", {"start": v(-40, -150) * mm, "end": v(-40, 150) * mm});
            skLineSegment(sketch, "E51.66.0.2", {"start": v(-38, -150) * mm, "end": v(-38, 150) * mm});
            skLineSegment(sketch, "E51.66.0.3", {"start": v(-40, -150) * mm, "end": v(-38, -150) * mm});
            skLineSegment(sketch, "E51.67.0.0", {"start": v(-44, 150) * mm, "end": v(-42, 150) * mm});
            skLineSegment(sketch, "E51.67.0.1", {"start": v(-44, -150) * mm, "end": v(-44, 150) * mm});
            skLineSegment(sketch, "E51.67.0.2", {"start": v(-42, -150) * mm, "end": v(-42, 150) * mm});
            skLineSegment(sketch, "E51.67.0.3", {"start": v(-44, -150) * mm, "end": v(-42, -150) * mm});
            skLineSegment(sketch, "E51.68.0.0", {"start": v(-48, 150) * mm, "end": v(-46, 150) * mm});
            skLineSegment(sketch, "E51.68.0.1", {"start": v(-48, -150) * mm, "end": v(-48, 150) * mm});
            skLineSegment(sketch, "E51.68.0.2", {"start": v(-46, -150) * mm, "end": v(-46, 150) * mm});
            skLineSegment(sketch, "E51.68.0.3", {"start": v(-48, -150) * mm, "end": v(-46, -150) * mm});
            skLineSegment(sketch, "E51.69.0.0", {"start": v(-52, 150) * mm, "end": v(-50, 150) * mm});
            skLineSegment(sketch, "E51.69.0.1", {"start": v(-52, -150) * mm, "end": v(-52, 150) * mm});
            skLineSegment(sketch, "E51.69.0.2", {"start": v(-50, -150) * mm, "end": v(-50, 150) * mm});
            skLineSegment(sketch, "E51.69.0.3", {"start": v(-52, -150) * mm, "end": v(-50, -150) * mm});
            skLineSegment(sketch, "E51.70.0.0", {"start": v(-56, 150) * mm, "end": v(-54, 150) * mm});
            skLineSegment(sketch, "E51.70.0.1", {"start": v(-56, -150) * mm, "end": v(-56, 150) * mm});
            skLineSegment(sketch, "E51.70.0.2", {"start": v(-54, -150) * mm, "end": v(-54, 150) * mm});
            skLineSegment(sketch, "E51.70.0.3", {"start": v(-56, -150) * mm, "end": v(-54, -150) * mm});
            skLineSegment(sketch, "E51.71.0.0", {"start": v(-60, 150) * mm, "end": v(-58, 150) * mm});
            skLineSegment(sketch, "E51.71.0.1", {"start": v(-60, -150) * mm, "end": v(-60, 150) * mm});
            skLineSegment(sketch, "E51.71.0.2", {"start": v(-58, -150) * mm, "end": v(-58, 150) * mm});
            skLineSegment(sketch, "E51.71.0.3", {"start": v(-60, -150) * mm, "end": v(-58, -150) * mm});
            skLineSegment(sketch, "E51.72.0.0", {"start": v(-64, 150) * mm, "end": v(-62, 150) * mm});
            skLineSegment(sketch, "E51.72.0.1", {"start": v(-64, -150) * mm, "end": v(-64, 150) * mm});
            skLineSegment(sketch, "E51.72.0.2", {"start": v(-62, -150) * mm, "end": v(-62, 150) * mm});
            skLineSegment(sketch, "E51.72.0.3", {"start": v(-64, -150) * mm, "end": v(-62, -150) * mm});
            skLineSegment(sketch, "E51.73.0.0", {"start": v(-68, 150) * mm, "end": v(-66, 150) * mm});
            skLineSegment(sketch, "E51.73.0.1", {"start": v(-68, -150) * mm, "end": v(-68, 150) * mm});
            skLineSegment(sketch, "E51.73.0.2", {"start": v(-66, -150) * mm, "end": v(-66, 150) * mm});
            skLineSegment(sketch, "E51.73.0.3", {"start": v(-68, -150) * mm, "end": v(-66, -150) * mm});
            skLineSegment(sketch, "E51.74.0.0", {"start": v(-72, 150) * mm, "end": v(-70, 150) * mm});
            skLineSegment(sketch, "E51.74.0.1", {"start": v(-72, -150) * mm, "end": v(-72, 150) * mm});
            skLineSegment(sketch, "E51.74.0.2", {"start": v(-70, -150) * mm, "end": v(-70, 150) * mm});
            skLineSegment(sketch, "E51.74.0.3", {"start": v(-72, -150) * mm, "end": v(-70, -150) * mm});
            skLineSegment(sketch, "E51.75.0.0", {"start": v(-76, 150) * mm, "end": v(-74, 150) * mm});
            skLineSegment(sketch, "E51.75.0.1", {"start": v(-76, -150) * mm, "end": v(-76, 150) * mm});
            skLineSegment(sketch, "E51.75.0.2", {"start": v(-74, -150) * mm, "end": v(-74, 150) * mm});
            skLineSegment(sketch, "E51.75.0.3", {"start": v(-76, -150) * mm, "end": v(-74, -150) * mm});
            skLineSegment(sketch, "E51.76.0.0", {"start": v(-80, 150) * mm, "end": v(-78, 150) * mm});
            skLineSegment(sketch, "E51.76.0.1", {"start": v(-80, -150) * mm, "end": v(-80, 150) * mm});
            skLineSegment(sketch, "E51.76.0.2", {"start": v(-78, -150) * mm, "end": v(-78, 150) * mm});
            skLineSegment(sketch, "E51.76.0.3", {"start": v(-80, -150) * mm, "end": v(-78, -150) * mm});
            skLineSegment(sketch, "E51.77.0.0", {"start": v(-84, 150) * mm, "end": v(-82, 150) * mm});
            skLineSegment(sketch, "E51.77.0.1", {"start": v(-84, -150) * mm, "end": v(-84, 150) * mm});
            skLineSegment(sketch, "E51.77.0.2", {"start": v(-82, -150) * mm, "end": v(-82, 150) * mm});
            skLineSegment(sketch, "E51.77.0.3", {"start": v(-84, -150) * mm, "end": v(-82, -150) * mm});
            skLineSegment(sketch, "E51.78.0.0", {"start": v(-88, 150) * mm, "end": v(-86, 150) * mm});
            skLineSegment(sketch, "E51.78.0.1", {"start": v(-88, -150) * mm, "end": v(-88, 150) * mm});
            skLineSegment(sketch, "E51.78.0.2", {"start": v(-86, -150) * mm, "end": v(-86, 150) * mm});
            skLineSegment(sketch, "E51.78.0.3", {"start": v(-88, -150) * mm, "end": v(-86, -150) * mm});
            skLineSegment(sketch, "E51.79.0.0", {"start": v(-92, 150) * mm, "end": v(-90, 150) * mm});
            skLineSegment(sketch, "E51.79.0.1", {"start": v(-92, -150) * mm, "end": v(-92, 150) * mm});
            skLineSegment(sketch, "E51.79.0.2", {"start": v(-90, -150) * mm, "end": v(-90, 150) * mm});
            skLineSegment(sketch, "E51.79.0.3", {"start": v(-92, -150) * mm, "end": v(-90, -150) * mm});
            skLineSegment(sketch, "E51.80.0.0", {"start": v(-96, 150) * mm, "end": v(-94, 150) * mm});
            skLineSegment(sketch, "E51.80.0.1", {"start": v(-96, -150) * mm, "end": v(-96, 150) * mm});
            skLineSegment(sketch, "E51.80.0.2", {"start": v(-94, -150) * mm, "end": v(-94, 150) * mm});
            skLineSegment(sketch, "E51.80.0.3", {"start": v(-96, -150) * mm, "end": v(-94, -150) * mm});
            skLineSegment(sketch, "E51.81.0.0", {"start": v(-100, 150) * mm, "end": v(-98, 150) * mm});
            skLineSegment(sketch, "E51.81.0.1", {"start": v(-100, -150) * mm, "end": v(-100, 150) * mm});
            skLineSegment(sketch, "E51.81.0.2", {"start": v(-98, -150) * mm, "end": v(-98, 150) * mm});
            skLineSegment(sketch, "E51.81.0.3", {"start": v(-100, -150) * mm, "end": v(-98, -150) * mm});
            skLineSegment(sketch, "E51.82.0.0", {"start": v(-104, 150) * mm, "end": v(-102, 150) * mm});
            skLineSegment(sketch, "E51.82.0.1", {"start": v(-104, -150) * mm, "end": v(-104, 150) * mm});
            skLineSegment(sketch, "E51.82.0.2", {"start": v(-102, -150) * mm, "end": v(-102, 150) * mm});
            skLineSegment(sketch, "E51.82.0.3", {"start": v(-104, -150) * mm, "end": v(-102, -150) * mm});
            skLineSegment(sketch, "E51.83.0.0", {"start": v(-108, 150) * mm, "end": v(-106, 150) * mm});
            skLineSegment(sketch, "E51.83.0.1", {"start": v(-108, -150) * mm, "end": v(-108, 150) * mm});
            skLineSegment(sketch, "E51.83.0.2", {"start": v(-106, -150) * mm, "end": v(-106, 150) * mm});
            skLineSegment(sketch, "E51.83.0.3", {"start": v(-108, -150) * mm, "end": v(-106, -150) * mm});
            skLineSegment(sketch, "E51.84.0.0", {"start": v(-112, 150) * mm, "end": v(-110, 150) * mm});
            skLineSegment(sketch, "E51.84.0.1", {"start": v(-112, -150) * mm, "end": v(-112, 150) * mm});
            skLineSegment(sketch, "E51.84.0.2", {"start": v(-110, -150) * mm, "end": v(-110, 150) * mm});
            skLineSegment(sketch, "E51.84.0.3", {"start": v(-112, -150) * mm, "end": v(-110, -150) * mm});
            skLineSegment(sketch, "E51.direction1", {"start": v(230, 150) * mm, "end": v(226, 150) * mm, "construction": true});
            skSolve(sketch);
        }
        {
            var Q0;
            Q0 = qSketchRegion(id + "F15", true);
            extrude(context, id + "F16", {"entities" : qUnion([Q0]), "operationType" : NewBodyOperationType.REMOVE, "oppositeDirection" : true, "depth" : 0.01 * mm, "offsetDistance" : 25 * mm});
        }
        {
            var Q0;
            Q0=makeQuery(id+"F2.opExtrude","SWEPT_FACE",FACE,{"disambiguationData":[OSD([sQuery(id+"F1.wireOp",EDGE,"E29.bottom")])]});
            var sketch = newSketch(context, id + "F17", { "sketchPlane" : qUnion([Q0])});
            skLineSegment(sketch, "E52.bottom", {"start": v(226, -125) * mm, "end": v(224, -125) * mm});
            skLineSegment(sketch, "E52.top", {"start": v(226, 125) * mm, "end": v(224, 125) * mm});
            skLineSegment(sketch, "E52.left", {"start": v(226, -125) * mm, "end": v(226, 125) * mm});
            skLineSegment(sketch, "E52.right", {"start": v(224, -125) * mm, "end": v(224, 125) * mm});
            skPoint(sketch, "E52.middle", {"position": v(225, 0) * mm});
            skLineSegment(sketch, "E53.1.0.0", {"start": v(220, -125) * mm, "end": v(220, 125) * mm});
            skLineSegment(sketch, "E53.1.0.1", {"start": v(222, -125) * mm, "end": v(222, 125) * mm});
            skLineSegment(sketch, "E53.1.0.2", {"start": v(222, -125) * mm, "end": v(220, -125) * mm});
            skLineSegment(sketch, "E53.1.0.3", {"start": v(222, 125) * mm, "end": v(220, 125) * mm});
            skLineSegment(sketch, "E53.2.0.0", {"start": v(216, -125) * mm, "end": v(216, 125) * mm});
            skLineSegment(sketch, "E53.2.0.1", {"start": v(218, -125) * mm, "end": v(218, 125) * mm});
            skLineSegment(sketch, "E53.2.0.2", {"start": v(218, -125) * mm, "end": v(216, -125) * mm});
            skLineSegment(sketch, "E53.2.0.3", {"start": v(218, 125) * mm, "end": v(216, 125) * mm});
            skLineSegment(sketch, "E53.3.0.0", {"start": v(212, -125) * mm, "end": v(212, 125) * mm});
            skLineSegment(sketch, "E53.3.0.1", {"start": v(214, -125) * mm, "end": v(214, 125) * mm});
            skLineSegment(sketch, "E53.3.0.2", {"start": v(214, -125) * mm, "end": v(212, -125) * mm});
            skLineSegment(sketch, "E53.3.0.3", {"start": v(214, 125) * mm, "end": v(212, 125) * mm});
            skLineSegment(sketch, "E53.4.0.0", {"start": v(208, -125) * mm, "end": v(208, 125) * mm});
            skLineSegment(sketch, "E53.4.0.1", {"start": v(210, -125) * mm, "end": v(210, 125) * mm});
            skLineSegment(sketch, "E53.4.0.2", {"start": v(210, -125) * mm, "end": v(208, -125) * mm});
            skLineSegment(sketch, "E53.4.0.3", {"start": v(210, 125) * mm, "end": v(208, 125) * mm});
            skLineSegment(sketch, "E53.5.0.0", {"start": v(204, -125) * mm, "end": v(204, 125) * mm});
            skLineSegment(sketch, "E53.5.0.1", {"start": v(206, -125) * mm, "end": v(206, 125) * mm});
            skLineSegment(sketch, "E53.5.0.2", {"start": v(206, -125) * mm, "end": v(204, -125) * mm});
            skLineSegment(sketch, "E53.5.0.3", {"start": v(206, 125) * mm, "end": v(204, 125) * mm});
            skLineSegment(sketch, "E53.6.0.0", {"start": v(200, -125) * mm, "end": v(200, 125) * mm});
            skLineSegment(sketch, "E53.6.0.1", {"start": v(202, -125) * mm, "end": v(202, 125) * mm});
            skLineSegment(sketch, "E53.6.0.2", {"start": v(202, -125) * mm, "end": v(200, -125) * mm});
            skLineSegment(sketch, "E53.6.0.3", {"start": v(202, 125) * mm, "end": v(200, 125) * mm});
            skLineSegment(sketch, "E53.7.0.0", {"start": v(196, -125) * mm, "end": v(196, 125) * mm});
            skLineSegment(sketch, "E53.7.0.1", {"start": v(198, -125) * mm, "end": v(198, 125) * mm});
            skLineSegment(sketch, "E53.7.0.2", {"start": v(198, -125) * mm, "end": v(196, -125) * mm});
            skLineSegment(sketch, "E53.7.0.3", {"start": v(198, 125) * mm, "end": v(196, 125) * mm});
            skLineSegment(sketch, "E53.8.0.0", {"start": v(192, -125) * mm, "end": v(192, 125) * mm});
            skLineSegment(sketch, "E53.8.0.1", {"start": v(194, -125) * mm, "end": v(194, 125) * mm});
            skLineSegment(sketch, "E53.8.0.2", {"start": v(194, -125) * mm, "end": v(192, -125) * mm});
            skLineSegment(sketch, "E53.8.0.3", {"start": v(194, 125) * mm, "end": v(192, 125) * mm});
            skLineSegment(sketch, "E53.9.0.0", {"start": v(188, -125) * mm, "end": v(188, 125) * mm});
            skLineSegment(sketch, "E53.9.0.1", {"start": v(190, -125) * mm, "end": v(190, 125) * mm});
            skLineSegment(sketch, "E53.9.0.2", {"start": v(190, -125) * mm, "end": v(188, -125) * mm});
            skLineSegment(sketch, "E53.9.0.3", {"start": v(190, 125) * mm, "end": v(188, 125) * mm});
            skLineSegment(sketch, "E53.10.0.0", {"start": v(184, -125) * mm, "end": v(184, 125) * mm});
            skLineSegment(sketch, "E53.10.0.1", {"start": v(186, -125) * mm, "end": v(186, 125) * mm});
            skLineSegment(sketch, "E53.10.0.2", {"start": v(186, -125) * mm, "end": v(184, -125) * mm});
            skLineSegment(sketch, "E53.10.0.3", {"start": v(186, 125) * mm, "end": v(184, 125) * mm});
            skLineSegment(sketch, "E53.11.0.0", {"start": v(180, -125) * mm, "end": v(180, 125) * mm});
            skLineSegment(sketch, "E53.11.0.1", {"start": v(182, -125) * mm, "end": v(182, 125) * mm});
            skLineSegment(sketch, "E53.11.0.2", {"start": v(182, -125) * mm, "end": v(180, -125) * mm});
            skLineSegment(sketch, "E53.11.0.3", {"start": v(182, 125) * mm, "end": v(180, 125) * mm});
            skLineSegment(sketch, "E53.12.0.0", {"start": v(176, -125) * mm, "end": v(176, 125) * mm});
            skLineSegment(sketch, "E53.12.0.1", {"start": v(178, -125) * mm, "end": v(178, 125) * mm});
            skLineSegment(sketch, "E53.12.0.2", {"start": v(178, -125) * mm, "end": v(176, -125) * mm});
            skLineSegment(sketch, "E53.12.0.3", {"start": v(178, 125) * mm, "end": v(176, 125) * mm});
            skLineSegment(sketch, "E53.13.0.0", {"start": v(172, -125) * mm, "end": v(172, 125) * mm});
            skLineSegment(sketch, "E53.13.0.1", {"start": v(174, -125) * mm, "end": v(174, 125) * mm});
            skLineSegment(sketch, "E53.13.0.2", {"start": v(174, -125) * mm, "end": v(172, -125) * mm});
            skLineSegment(sketch, "E53.13.0.3", {"start": v(174, 125) * mm, "end": v(172, 125) * mm});
            skLineSegment(sketch, "E53.14.0.0", {"start": v(168, -125) * mm, "end": v(168, 125) * mm});
            skLineSegment(sketch, "E53.14.0.1", {"start": v(170, -125) * mm, "end": v(170, 125) * mm});
            skLineSegment(sketch, "E53.14.0.2", {"start": v(170, -125) * mm, "end": v(168, -125) * mm});
            skLineSegment(sketch, "E53.14.0.3", {"start": v(170, 125) * mm, "end": v(168, 125) * mm});
            skLineSegment(sketch, "E53.15.0.0", {"start": v(164, -125) * mm, "end": v(164, 125) * mm});
            skLineSegment(sketch, "E53.15.0.1", {"start": v(166, -125) * mm, "end": v(166, 125) * mm});
            skLineSegment(sketch, "E53.15.0.2", {"start": v(166, -125) * mm, "end": v(164, -125) * mm});
            skLineSegment(sketch, "E53.15.0.3", {"start": v(166, 125) * mm, "end": v(164, 125) * mm});
            skLineSegment(sketch, "E53.16.0.0", {"start": v(160, -125) * mm, "end": v(160, 125) * mm});
            skLineSegment(sketch, "E53.16.0.1", {"start": v(162, -125) * mm, "end": v(162, 125) * mm});
            skLineSegment(sketch, "E53.16.0.2", {"start": v(162, -125) * mm, "end": v(160, -125) * mm});
            skLineSegment(sketch, "E53.16.0.3", {"start": v(162, 125) * mm, "end": v(160, 125) * mm});
            skLineSegment(sketch, "E53.17.0.0", {"start": v(156, -125) * mm, "end": v(156, 125) * mm});
            skLineSegment(sketch, "E53.17.0.1", {"start": v(158, -125) * mm, "end": v(158, 125) * mm});
            skLineSegment(sketch, "E53.17.0.2", {"start": v(158, -125) * mm, "end": v(156, -125) * mm});
            skLineSegment(sketch, "E53.17.0.3", {"start": v(158, 125) * mm, "end": v(156, 125) * mm});
            skLineSegment(sketch, "E53.18.0.0", {"start": v(152, -125) * mm, "end": v(152, 125) * mm});
            skLineSegment(sketch, "E53.18.0.1", {"start": v(154, -125) * mm, "end": v(154, 125) * mm});
            skLineSegment(sketch, "E53.18.0.2", {"start": v(154, -125) * mm, "end": v(152, -125) * mm});
            skLineSegment(sketch, "E53.18.0.3", {"start": v(154, 125) * mm, "end": v(152, 125) * mm});
            skLineSegment(sketch, "E53.19.0.0", {"start": v(148, -125) * mm, "end": v(148, 125) * mm});
            skLineSegment(sketch, "E53.19.0.1", {"start": v(150, -125) * mm, "end": v(150, 125) * mm});
            skLineSegment(sketch, "E53.19.0.2", {"start": v(150, -125) * mm, "end": v(148, -125) * mm});
            skLineSegment(sketch, "E53.19.0.3", {"start": v(150, 125) * mm, "end": v(148, 125) * mm});
            skLineSegment(sketch, "E53.20.0.0", {"start": v(144, -125) * mm, "end": v(144, 125) * mm});
            skLineSegment(sketch, "E53.20.0.1", {"start": v(146, -125) * mm, "end": v(146, 125) * mm});
            skLineSegment(sketch, "E53.20.0.2", {"start": v(146, -125) * mm, "end": v(144, -125) * mm});
            skLineSegment(sketch, "E53.20.0.3", {"start": v(146, 125) * mm, "end": v(144, 125) * mm});
            skLineSegment(sketch, "E53.21.0.0", {"start": v(140, -125) * mm, "end": v(140, 125) * mm});
            skLineSegment(sketch, "E53.21.0.1", {"start": v(142, -125) * mm, "end": v(142, 125) * mm});
            skLineSegment(sketch, "E53.21.0.2", {"start": v(142, -125) * mm, "end": v(140, -125) * mm});
            skLineSegment(sketch, "E53.21.0.3", {"start": v(142, 125) * mm, "end": v(140, 125) * mm});
            skLineSegment(sketch, "E53.22.0.0", {"start": v(136, -125) * mm, "end": v(136, 125) * mm});
            skLineSegment(sketch, "E53.22.0.1", {"start": v(138, -125) * mm, "end": v(138, 125) * mm});
            skLineSegment(sketch, "E53.22.0.2", {"start": v(138, -125) * mm, "end": v(136, -125) * mm});
            skLineSegment(sketch, "E53.22.0.3", {"start": v(138, 125) * mm, "end": v(136, 125) * mm});
            skLineSegment(sketch, "E53.23.0.0", {"start": v(132, -125) * mm, "end": v(132, 125) * mm});
            skLineSegment(sketch, "E53.23.0.1", {"start": v(134, -125) * mm, "end": v(134, 125) * mm});
            skLineSegment(sketch, "E53.23.0.2", {"start": v(134, -125) * mm, "end": v(132, -125) * mm});
            skLineSegment(sketch, "E53.23.0.3", {"start": v(134, 125) * mm, "end": v(132, 125) * mm});
            skLineSegment(sketch, "E53.24.0.0", {"start": v(128, -125) * mm, "end": v(128, 125) * mm});
            skLineSegment(sketch, "E53.24.0.1", {"start": v(130, -125) * mm, "end": v(130, 125) * mm});
            skLineSegment(sketch, "E53.24.0.2", {"start": v(130, -125) * mm, "end": v(128, -125) * mm});
            skLineSegment(sketch, "E53.24.0.3", {"start": v(130, 125) * mm, "end": v(128, 125) * mm});
            skLineSegment(sketch, "E53.25.0.0", {"start": v(124, -125) * mm, "end": v(124, 125) * mm});
            skLineSegment(sketch, "E53.25.0.1", {"start": v(126, -125) * mm, "end": v(126, 125) * mm});
            skLineSegment(sketch, "E53.25.0.2", {"start": v(126, -125) * mm, "end": v(124, -125) * mm});
            skLineSegment(sketch, "E53.25.0.3", {"start": v(126, 125) * mm, "end": v(124, 125) * mm});
            skLineSegment(sketch, "E53.26.0.0", {"start": v(120, -125) * mm, "end": v(120, 125) * mm});
            skLineSegment(sketch, "E53.26.0.1", {"start": v(122, -125) * mm, "end": v(122, 125) * mm});
            skLineSegment(sketch, "E53.26.0.2", {"start": v(122, -125) * mm, "end": v(120, -125) * mm});
            skLineSegment(sketch, "E53.26.0.3", {"start": v(122, 125) * mm, "end": v(120, 125) * mm});
            skLineSegment(sketch, "E53.27.0.0", {"start": v(116, -125) * mm, "end": v(116, 125) * mm});
            skLineSegment(sketch, "E53.27.0.1", {"start": v(118, -125) * mm, "end": v(118, 125) * mm});
            skLineSegment(sketch, "E53.27.0.2", {"start": v(118, -125) * mm, "end": v(116, -125) * mm});
            skLineSegment(sketch, "E53.27.0.3", {"start": v(118, 125) * mm, "end": v(116, 125) * mm});
            skLineSegment(sketch, "E53.28.0.0", {"start": v(112, -125) * mm, "end": v(112, 125) * mm});
            skLineSegment(sketch, "E53.28.0.1", {"start": v(114, -125) * mm, "end": v(114, 125) * mm});
            skLineSegment(sketch, "E53.28.0.2", {"start": v(114, -125) * mm, "end": v(112, -125) * mm});
            skLineSegment(sketch, "E53.28.0.3", {"start": v(114, 125) * mm, "end": v(112, 125) * mm});
            skLineSegment(sketch, "E53.29.0.0", {"start": v(108, -125) * mm, "end": v(108, 125) * mm});
            skLineSegment(sketch, "E53.29.0.1", {"start": v(110, -125) * mm, "end": v(110, 125) * mm});
            skLineSegment(sketch, "E53.29.0.2", {"start": v(110, -125) * mm, "end": v(108, -125) * mm});
            skLineSegment(sketch, "E53.29.0.3", {"start": v(110, 125) * mm, "end": v(108, 125) * mm});
            skLineSegment(sketch, "E53.30.0.0", {"start": v(104, -125) * mm, "end": v(104, 125) * mm});
            skLineSegment(sketch, "E53.30.0.1", {"start": v(106, -125) * mm, "end": v(106, 125) * mm});
            skLineSegment(sketch, "E53.30.0.2", {"start": v(106, -125) * mm, "end": v(104, -125) * mm});
            skLineSegment(sketch, "E53.30.0.3", {"start": v(106, 125) * mm, "end": v(104, 125) * mm});
            skLineSegment(sketch, "E53.31.0.0", {"start": v(100, -125) * mm, "end": v(100, 125) * mm});
            skLineSegment(sketch, "E53.31.0.1", {"start": v(102, -125) * mm, "end": v(102, 125) * mm});
            skLineSegment(sketch, "E53.31.0.2", {"start": v(102, -125) * mm, "end": v(100, -125) * mm});
            skLineSegment(sketch, "E53.31.0.3", {"start": v(102, 125) * mm, "end": v(100, 125) * mm});
            skLineSegment(sketch, "E53.32.0.0", {"start": v(96, -125) * mm, "end": v(96, 125) * mm});
            skLineSegment(sketch, "E53.32.0.1", {"start": v(98, -125) * mm, "end": v(98, 125) * mm});
            skLineSegment(sketch, "E53.32.0.2", {"start": v(98, -125) * mm, "end": v(96, -125) * mm});
            skLineSegment(sketch, "E53.32.0.3", {"start": v(98, 125) * mm, "end": v(96, 125) * mm});
            skLineSegment(sketch, "E53.33.0.0", {"start": v(92, -125) * mm, "end": v(92, 125) * mm});
            skLineSegment(sketch, "E53.33.0.1", {"start": v(94, -125) * mm, "end": v(94, 125) * mm});
            skLineSegment(sketch, "E53.33.0.2", {"start": v(94, -125) * mm, "end": v(92, -125) * mm});
            skLineSegment(sketch, "E53.33.0.3", {"start": v(94, 125) * mm, "end": v(92, 125) * mm});
            skLineSegment(sketch, "E53.34.0.0", {"start": v(88, -125) * mm, "end": v(88, 125) * mm});
            skLineSegment(sketch, "E53.34.0.1", {"start": v(90, -125) * mm, "end": v(90, 125) * mm});
            skLineSegment(sketch, "E53.34.0.2", {"start": v(90, -125) * mm, "end": v(88, -125) * mm});
            skLineSegment(sketch, "E53.34.0.3", {"start": v(90, 125) * mm, "end": v(88, 125) * mm});
            skLineSegment(sketch, "E53.35.0.0", {"start": v(84, -125) * mm, "end": v(84, 125) * mm});
            skLineSegment(sketch, "E53.35.0.1", {"start": v(86, -125) * mm, "end": v(86, 125) * mm});
            skLineSegment(sketch, "E53.35.0.2", {"start": v(86, -125) * mm, "end": v(84, -125) * mm});
            skLineSegment(sketch, "E53.35.0.3", {"start": v(86, 125) * mm, "end": v(84, 125) * mm});
            skLineSegment(sketch, "E53.36.0.0", {"start": v(80, -125) * mm, "end": v(80, 125) * mm});
            skLineSegment(sketch, "E53.36.0.1", {"start": v(82, -125) * mm, "end": v(82, 125) * mm});
            skLineSegment(sketch, "E53.36.0.2", {"start": v(82, -125) * mm, "end": v(80, -125) * mm});
            skLineSegment(sketch, "E53.36.0.3", {"start": v(82, 125) * mm, "end": v(80, 125) * mm});
            skLineSegment(sketch, "E53.37.0.0", {"start": v(76, -125) * mm, "end": v(76, 125) * mm});
            skLineSegment(sketch, "E53.37.0.1", {"start": v(78, -125) * mm, "end": v(78, 125) * mm});
            skLineSegment(sketch, "E53.37.0.2", {"start": v(78, -125) * mm, "end": v(76, -125) * mm});
            skLineSegment(sketch, "E53.37.0.3", {"start": v(78, 125) * mm, "end": v(76, 125) * mm});
            skLineSegment(sketch, "E53.38.0.0", {"start": v(72, -125) * mm, "end": v(72, 125) * mm});
            skLineSegment(sketch, "E53.38.0.1", {"start": v(74, -125) * mm, "end": v(74, 125) * mm});
            skLineSegment(sketch, "E53.38.0.2", {"start": v(74, -125) * mm, "end": v(72, -125) * mm});
            skLineSegment(sketch, "E53.38.0.3", {"start": v(74, 125) * mm, "end": v(72, 125) * mm});
            skLineSegment(sketch, "E53.39.0.0", {"start": v(68, -125) * mm, "end": v(68, 125) * mm});
            skLineSegment(sketch, "E53.39.0.1", {"start": v(70, -125) * mm, "end": v(70, 125) * mm});
            skLineSegment(sketch, "E53.39.0.2", {"start": v(70, -125) * mm, "end": v(68, -125) * mm});
            skLineSegment(sketch, "E53.39.0.3", {"start": v(70, 125) * mm, "end": v(68, 125) * mm});
            skLineSegment(sketch, "E53.40.0.0", {"start": v(64, -125) * mm, "end": v(64, 125) * mm});
            skLineSegment(sketch, "E53.40.0.1", {"start": v(66, -125) * mm, "end": v(66, 125) * mm});
            skLineSegment(sketch, "E53.40.0.2", {"start": v(66, -125) * mm, "end": v(64, -125) * mm});
            skLineSegment(sketch, "E53.40.0.3", {"start": v(66, 125) * mm, "end": v(64, 125) * mm});
            skLineSegment(sketch, "E53.41.0.0", {"start": v(60, -125) * mm, "end": v(60, 125) * mm});
            skLineSegment(sketch, "E53.41.0.1", {"start": v(62, -125) * mm, "end": v(62, 125) * mm});
            skLineSegment(sketch, "E53.41.0.2", {"start": v(62, -125) * mm, "end": v(60, -125) * mm});
            skLineSegment(sketch, "E53.41.0.3", {"start": v(62, 125) * mm, "end": v(60, 125) * mm});
            skLineSegment(sketch, "E53.42.0.0", {"start": v(56, -125) * mm, "end": v(56, 125) * mm});
            skLineSegment(sketch, "E53.42.0.1", {"start": v(58, -125) * mm, "end": v(58, 125) * mm});
            skLineSegment(sketch, "E53.42.0.2", {"start": v(58, -125) * mm, "end": v(56, -125) * mm});
            skLineSegment(sketch, "E53.42.0.3", {"start": v(58, 125) * mm, "end": v(56, 125) * mm});
            skLineSegment(sketch, "E53.43.0.0", {"start": v(52, -125) * mm, "end": v(52, 125) * mm});
            skLineSegment(sketch, "E53.43.0.1", {"start": v(54, -125) * mm, "end": v(54, 125) * mm});
            skLineSegment(sketch, "E53.43.0.2", {"start": v(54, -125) * mm, "end": v(52, -125) * mm});
            skLineSegment(sketch, "E53.43.0.3", {"start": v(54, 125) * mm, "end": v(52, 125) * mm});
            skLineSegment(sketch, "E53.44.0.0", {"start": v(48, -125) * mm, "end": v(48, 125) * mm});
            skLineSegment(sketch, "E53.44.0.1", {"start": v(50, -125) * mm, "end": v(50, 125) * mm});
            skLineSegment(sketch, "E53.44.0.2", {"start": v(50, -125) * mm, "end": v(48, -125) * mm});
            skLineSegment(sketch, "E53.44.0.3", {"start": v(50, 125) * mm, "end": v(48, 125) * mm});
            skLineSegment(sketch, "E53.45.0.0", {"start": v(44, -125) * mm, "end": v(44, 125) * mm});
            skLineSegment(sketch, "E53.45.0.1", {"start": v(46, -125) * mm, "end": v(46, 125) * mm});
            skLineSegment(sketch, "E53.45.0.2", {"start": v(46, -125) * mm, "end": v(44, -125) * mm});
            skLineSegment(sketch, "E53.45.0.3", {"start": v(46, 125) * mm, "end": v(44, 125) * mm});
            skLineSegment(sketch, "E53.46.0.0", {"start": v(40, -125) * mm, "end": v(40, 125) * mm});
            skLineSegment(sketch, "E53.46.0.1", {"start": v(42, -125) * mm, "end": v(42, 125) * mm});
            skLineSegment(sketch, "E53.46.0.2", {"start": v(42, -125) * mm, "end": v(40, -125) * mm});
            skLineSegment(sketch, "E53.46.0.3", {"start": v(42, 125) * mm, "end": v(40, 125) * mm});
            skLineSegment(sketch, "E53.47.0.0", {"start": v(36, -125) * mm, "end": v(36, 125) * mm});
            skLineSegment(sketch, "E53.47.0.1", {"start": v(38, -125) * mm, "end": v(38, 125) * mm});
            skLineSegment(sketch, "E53.47.0.2", {"start": v(38, -125) * mm, "end": v(36, -125) * mm});
            skLineSegment(sketch, "E53.47.0.3", {"start": v(38, 125) * mm, "end": v(36, 125) * mm});
            skLineSegment(sketch, "E53.48.0.0", {"start": v(32, -125) * mm, "end": v(32, 125) * mm});
            skLineSegment(sketch, "E53.48.0.1", {"start": v(34, -125) * mm, "end": v(34, 125) * mm});
            skLineSegment(sketch, "E53.48.0.2", {"start": v(34, -125) * mm, "end": v(32, -125) * mm});
            skLineSegment(sketch, "E53.48.0.3", {"start": v(34, 125) * mm, "end": v(32, 125) * mm});
            skLineSegment(sketch, "E53.49.0.0", {"start": v(28, -125) * mm, "end": v(28, 125) * mm});
            skLineSegment(sketch, "E53.49.0.1", {"start": v(30, -125) * mm, "end": v(30, 125) * mm});
            skLineSegment(sketch, "E53.49.0.2", {"start": v(30, -125) * mm, "end": v(28, -125) * mm});
            skLineSegment(sketch, "E53.49.0.3", {"start": v(30, 125) * mm, "end": v(28, 125) * mm});
            skLineSegment(sketch, "E53.50.0.0", {"start": v(24, -125) * mm, "end": v(24, 125) * mm});
            skLineSegment(sketch, "E53.50.0.1", {"start": v(26, -125) * mm, "end": v(26, 125) * mm});
            skLineSegment(sketch, "E53.50.0.2", {"start": v(26, -125) * mm, "end": v(24, -125) * mm});
            skLineSegment(sketch, "E53.50.0.3", {"start": v(26, 125) * mm, "end": v(24, 125) * mm});
            skLineSegment(sketch, "E53.51.0.0", {"start": v(20, -125) * mm, "end": v(20, 125) * mm});
            skLineSegment(sketch, "E53.51.0.1", {"start": v(22, -125) * mm, "end": v(22, 125) * mm});
            skLineSegment(sketch, "E53.51.0.2", {"start": v(22, -125) * mm, "end": v(20, -125) * mm});
            skLineSegment(sketch, "E53.51.0.3", {"start": v(22, 125) * mm, "end": v(20, 125) * mm});
            skLineSegment(sketch, "E53.52.0.0", {"start": v(16, -125) * mm, "end": v(16, 125) * mm});
            skLineSegment(sketch, "E53.52.0.1", {"start": v(18, -125) * mm, "end": v(18, 125) * mm});
            skLineSegment(sketch, "E53.52.0.2", {"start": v(18, -125) * mm, "end": v(16, -125) * mm});
            skLineSegment(sketch, "E53.52.0.3", {"start": v(18, 125) * mm, "end": v(16, 125) * mm});
            skLineSegment(sketch, "E53.53.0.0", {"start": v(12, -125) * mm, "end": v(12, 125) * mm});
            skLineSegment(sketch, "E53.53.0.1", {"start": v(14, -125) * mm, "end": v(14, 125) * mm});
            skLineSegment(sketch, "E53.53.0.2", {"start": v(14, -125) * mm, "end": v(12, -125) * mm});
            skLineSegment(sketch, "E53.53.0.3", {"start": v(14, 125) * mm, "end": v(12, 125) * mm});
            skLineSegment(sketch, "E53.54.0.0", {"start": v(8, -125) * mm, "end": v(8, 125) * mm});
            skLineSegment(sketch, "E53.54.0.1", {"start": v(10, -125) * mm, "end": v(10, 125) * mm});
            skLineSegment(sketch, "E53.54.0.2", {"start": v(10, -125) * mm, "end": v(8, -125) * mm});
            skLineSegment(sketch, "E53.54.0.3", {"start": v(10, 125) * mm, "end": v(8, 125) * mm});
            skLineSegment(sketch, "E53.55.0.0", {"start": v(4, -125) * mm, "end": v(4, 125) * mm});
            skLineSegment(sketch, "E53.55.0.1", {"start": v(6, -125) * mm, "end": v(6, 125) * mm});
            skLineSegment(sketch, "E53.55.0.2", {"start": v(6, -125) * mm, "end": v(4, -125) * mm});
            skLineSegment(sketch, "E53.55.0.3", {"start": v(6, 125) * mm, "end": v(4, 125) * mm});
            skLineSegment(sketch, "E53.56.0.0", {"start": v(0, -125) * mm, "end": v(0, 125) * mm});
            skLineSegment(sketch, "E53.56.0.1", {"start": v(2, -125) * mm, "end": v(2, 125) * mm});
            skLineSegment(sketch, "E53.56.0.2", {"start": v(2, -125) * mm, "end": v(0, -125) * mm});
            skLineSegment(sketch, "E53.56.0.3", {"start": v(2, 125) * mm, "end": v(0, 125) * mm});
            skLineSegment(sketch, "E53.57.0.0", {"start": v(-4, -125) * mm, "end": v(-4, 125) * mm});
            skLineSegment(sketch, "E53.57.0.1", {"start": v(-2, -125) * mm, "end": v(-2, 125) * mm});
            skLineSegment(sketch, "E53.57.0.2", {"start": v(-2, -125) * mm, "end": v(-4, -125) * mm});
            skLineSegment(sketch, "E53.57.0.3", {"start": v(-2, 125) * mm, "end": v(-4, 125) * mm});
            skLineSegment(sketch, "E53.58.0.0", {"start": v(-8, -125) * mm, "end": v(-8, 125) * mm});
            skLineSegment(sketch, "E53.58.0.1", {"start": v(-6, -125) * mm, "end": v(-6, 125) * mm});
            skLineSegment(sketch, "E53.58.0.2", {"start": v(-6, -125) * mm, "end": v(-8, -125) * mm});
            skLineSegment(sketch, "E53.58.0.3", {"start": v(-6, 125) * mm, "end": v(-8, 125) * mm});
            skLineSegment(sketch, "E53.59.0.0", {"start": v(-12, -125) * mm, "end": v(-12, 125) * mm});
            skLineSegment(sketch, "E53.59.0.1", {"start": v(-10, -125) * mm, "end": v(-10, 125) * mm});
            skLineSegment(sketch, "E53.59.0.2", {"start": v(-10, -125) * mm, "end": v(-12, -125) * mm});
            skLineSegment(sketch, "E53.59.0.3", {"start": v(-10, 125) * mm, "end": v(-12, 125) * mm});
            skLineSegment(sketch, "E53.60.0.0", {"start": v(-16, -125) * mm, "end": v(-16, 125) * mm});
            skLineSegment(sketch, "E53.60.0.1", {"start": v(-14, -125) * mm, "end": v(-14, 125) * mm});
            skLineSegment(sketch, "E53.60.0.2", {"start": v(-14, -125) * mm, "end": v(-16, -125) * mm});
            skLineSegment(sketch, "E53.60.0.3", {"start": v(-14, 125) * mm, "end": v(-16, 125) * mm});
            skLineSegment(sketch, "E53.61.0.0", {"start": v(-20, -125) * mm, "end": v(-20, 125) * mm});
            skLineSegment(sketch, "E53.61.0.1", {"start": v(-18, -125) * mm, "end": v(-18, 125) * mm});
            skLineSegment(sketch, "E53.61.0.2", {"start": v(-18, -125) * mm, "end": v(-20, -125) * mm});
            skLineSegment(sketch, "E53.61.0.3", {"start": v(-18, 125) * mm, "end": v(-20, 125) * mm});
            skLineSegment(sketch, "E53.62.0.0", {"start": v(-24, -125) * mm, "end": v(-24, 125) * mm});
            skLineSegment(sketch, "E53.62.0.1", {"start": v(-22, -125) * mm, "end": v(-22, 125) * mm});
            skLineSegment(sketch, "E53.62.0.2", {"start": v(-22, -125) * mm, "end": v(-24, -125) * mm});
            skLineSegment(sketch, "E53.62.0.3", {"start": v(-22, 125) * mm, "end": v(-24, 125) * mm});
            skLineSegment(sketch, "E53.63.0.0", {"start": v(-28, -125) * mm, "end": v(-28, 125) * mm});
            skLineSegment(sketch, "E53.63.0.1", {"start": v(-26, -125) * mm, "end": v(-26, 125) * mm});
            skLineSegment(sketch, "E53.63.0.2", {"start": v(-26, -125) * mm, "end": v(-28, -125) * mm});
            skLineSegment(sketch, "E53.63.0.3", {"start": v(-26, 125) * mm, "end": v(-28, 125) * mm});
            skLineSegment(sketch, "E53.64.0.0", {"start": v(-32, -125) * mm, "end": v(-32, 125) * mm});
            skLineSegment(sketch, "E53.64.0.1", {"start": v(-30, -125) * mm, "end": v(-30, 125) * mm});
            skLineSegment(sketch, "E53.64.0.2", {"start": v(-30, -125) * mm, "end": v(-32, -125) * mm});
            skLineSegment(sketch, "E53.64.0.3", {"start": v(-30, 125) * mm, "end": v(-32, 125) * mm});
            skLineSegment(sketch, "E53.65.0.0", {"start": v(-36, -125) * mm, "end": v(-36, 125) * mm});
            skLineSegment(sketch, "E53.65.0.1", {"start": v(-34, -125) * mm, "end": v(-34, 125) * mm});
            skLineSegment(sketch, "E53.65.0.2", {"start": v(-34, -125) * mm, "end": v(-36, -125) * mm});
            skLineSegment(sketch, "E53.65.0.3", {"start": v(-34, 125) * mm, "end": v(-36, 125) * mm});
            skLineSegment(sketch, "E53.66.0.0", {"start": v(-40, -125) * mm, "end": v(-40, 125) * mm});
            skLineSegment(sketch, "E53.66.0.1", {"start": v(-38, -125) * mm, "end": v(-38, 125) * mm});
            skLineSegment(sketch, "E53.66.0.2", {"start": v(-38, -125) * mm, "end": v(-40, -125) * mm});
            skLineSegment(sketch, "E53.66.0.3", {"start": v(-38, 125) * mm, "end": v(-40, 125) * mm});
            skLineSegment(sketch, "E53.67.0.0", {"start": v(-44, -125) * mm, "end": v(-44, 125) * mm});
            skLineSegment(sketch, "E53.67.0.1", {"start": v(-42, -125) * mm, "end": v(-42, 125) * mm});
            skLineSegment(sketch, "E53.67.0.2", {"start": v(-42, -125) * mm, "end": v(-44, -125) * mm});
            skLineSegment(sketch, "E53.67.0.3", {"start": v(-42, 125) * mm, "end": v(-44, 125) * mm});
            skLineSegment(sketch, "E53.68.0.0", {"start": v(-48, -125) * mm, "end": v(-48, 125) * mm});
            skLineSegment(sketch, "E53.68.0.1", {"start": v(-46, -125) * mm, "end": v(-46, 125) * mm});
            skLineSegment(sketch, "E53.68.0.2", {"start": v(-46, -125) * mm, "end": v(-48, -125) * mm});
            skLineSegment(sketch, "E53.68.0.3", {"start": v(-46, 125) * mm, "end": v(-48, 125) * mm});
            skLineSegment(sketch, "E53.69.0.0", {"start": v(-52, -125) * mm, "end": v(-52, 125) * mm});
            skLineSegment(sketch, "E53.69.0.1", {"start": v(-50, -125) * mm, "end": v(-50, 125) * mm});
            skLineSegment(sketch, "E53.69.0.2", {"start": v(-50, -125) * mm, "end": v(-52, -125) * mm});
            skLineSegment(sketch, "E53.69.0.3", {"start": v(-50, 125) * mm, "end": v(-52, 125) * mm});
            skLineSegment(sketch, "E53.70.0.0", {"start": v(-56, -125) * mm, "end": v(-56, 125) * mm});
            skLineSegment(sketch, "E53.70.0.1", {"start": v(-54, -125) * mm, "end": v(-54, 125) * mm});
            skLineSegment(sketch, "E53.70.0.2", {"start": v(-54, -125) * mm, "end": v(-56, -125) * mm});
            skLineSegment(sketch, "E53.70.0.3", {"start": v(-54, 125) * mm, "end": v(-56, 125) * mm});
            skLineSegment(sketch, "E53.71.0.0", {"start": v(-60, -125) * mm, "end": v(-60, 125) * mm});
            skLineSegment(sketch, "E53.71.0.1", {"start": v(-58, -125) * mm, "end": v(-58, 125) * mm});
            skLineSegment(sketch, "E53.71.0.2", {"start": v(-58, -125) * mm, "end": v(-60, -125) * mm});
            skLineSegment(sketch, "E53.71.0.3", {"start": v(-58, 125) * mm, "end": v(-60, 125) * mm});
            skLineSegment(sketch, "E53.72.0.0", {"start": v(-64, -125) * mm, "end": v(-64, 125) * mm});
            skLineSegment(sketch, "E53.72.0.1", {"start": v(-62, -125) * mm, "end": v(-62, 125) * mm});
            skLineSegment(sketch, "E53.72.0.2", {"start": v(-62, -125) * mm, "end": v(-64, -125) * mm});
            skLineSegment(sketch, "E53.72.0.3", {"start": v(-62, 125) * mm, "end": v(-64, 125) * mm});
            skLineSegment(sketch, "E53.73.0.0", {"start": v(-68, -125) * mm, "end": v(-68, 125) * mm});
            skLineSegment(sketch, "E53.73.0.1", {"start": v(-66, -125) * mm, "end": v(-66, 125) * mm});
            skLineSegment(sketch, "E53.73.0.2", {"start": v(-66, -125) * mm, "end": v(-68, -125) * mm});
            skLineSegment(sketch, "E53.73.0.3", {"start": v(-66, 125) * mm, "end": v(-68, 125) * mm});
            skLineSegment(sketch, "E53.74.0.0", {"start": v(-72, -125) * mm, "end": v(-72, 125) * mm});
            skLineSegment(sketch, "E53.74.0.1", {"start": v(-70, -125) * mm, "end": v(-70, 125) * mm});
            skLineSegment(sketch, "E53.74.0.2", {"start": v(-70, -125) * mm, "end": v(-72, -125) * mm});
            skLineSegment(sketch, "E53.74.0.3", {"start": v(-70, 125) * mm, "end": v(-72, 125) * mm});
            skLineSegment(sketch, "E53.75.0.0", {"start": v(-76, -125) * mm, "end": v(-76, 125) * mm});
            skLineSegment(sketch, "E53.75.0.1", {"start": v(-74, -125) * mm, "end": v(-74, 125) * mm});
            skLineSegment(sketch, "E53.75.0.2", {"start": v(-74, -125) * mm, "end": v(-76, -125) * mm});
            skLineSegment(sketch, "E53.75.0.3", {"start": v(-74, 125) * mm, "end": v(-76, 125) * mm});
            skLineSegment(sketch, "E53.76.0.0", {"start": v(-80, -125) * mm, "end": v(-80, 125) * mm});
            skLineSegment(sketch, "E53.76.0.1", {"start": v(-78, -125) * mm, "end": v(-78, 125) * mm});
            skLineSegment(sketch, "E53.76.0.2", {"start": v(-78, -125) * mm, "end": v(-80, -125) * mm});
            skLineSegment(sketch, "E53.76.0.3", {"start": v(-78, 125) * mm, "end": v(-80, 125) * mm});
            skLineSegment(sketch, "E53.77.0.0", {"start": v(-84, -125) * mm, "end": v(-84, 125) * mm});
            skLineSegment(sketch, "E53.77.0.1", {"start": v(-82, -125) * mm, "end": v(-82, 125) * mm});
            skLineSegment(sketch, "E53.77.0.2", {"start": v(-82, -125) * mm, "end": v(-84, -125) * mm});
            skLineSegment(sketch, "E53.77.0.3", {"start": v(-82, 125) * mm, "end": v(-84, 125) * mm});
            skLineSegment(sketch, "E53.78.0.0", {"start": v(-88, -125) * mm, "end": v(-88, 125) * mm});
            skLineSegment(sketch, "E53.78.0.1", {"start": v(-86, -125) * mm, "end": v(-86, 125) * mm});
            skLineSegment(sketch, "E53.78.0.2", {"start": v(-86, -125) * mm, "end": v(-88, -125) * mm});
            skLineSegment(sketch, "E53.78.0.3", {"start": v(-86, 125) * mm, "end": v(-88, 125) * mm});
            skLineSegment(sketch, "E53.79.0.0", {"start": v(-92, -125) * mm, "end": v(-92, 125) * mm});
            skLineSegment(sketch, "E53.79.0.1", {"start": v(-90, -125) * mm, "end": v(-90, 125) * mm});
            skLineSegment(sketch, "E53.79.0.2", {"start": v(-90, -125) * mm, "end": v(-92, -125) * mm});
            skLineSegment(sketch, "E53.79.0.3", {"start": v(-90, 125) * mm, "end": v(-92, 125) * mm});
            skLineSegment(sketch, "E53.80.0.0", {"start": v(-96, -125) * mm, "end": v(-96, 125) * mm});
            skLineSegment(sketch, "E53.80.0.1", {"start": v(-94, -125) * mm, "end": v(-94, 125) * mm});
            skLineSegment(sketch, "E53.80.0.2", {"start": v(-94, -125) * mm, "end": v(-96, -125) * mm});
            skLineSegment(sketch, "E53.80.0.3", {"start": v(-94, 125) * mm, "end": v(-96, 125) * mm});
            skLineSegment(sketch, "E53.81.0.0", {"start": v(-100, -125) * mm, "end": v(-100, 125) * mm});
            skLineSegment(sketch, "E53.81.0.1", {"start": v(-98, -125) * mm, "end": v(-98, 125) * mm});
            skLineSegment(sketch, "E53.81.0.2", {"start": v(-98, -125) * mm, "end": v(-100, -125) * mm});
            skLineSegment(sketch, "E53.81.0.3", {"start": v(-98, 125) * mm, "end": v(-100, 125) * mm});
            skLineSegment(sketch, "E53.82.0.0", {"start": v(-104, -125) * mm, "end": v(-104, 125) * mm});
            skLineSegment(sketch, "E53.82.0.1", {"start": v(-102, -125) * mm, "end": v(-102, 125) * mm});
            skLineSegment(sketch, "E53.82.0.2", {"start": v(-102, -125) * mm, "end": v(-104, -125) * mm});
            skLineSegment(sketch, "E53.82.0.3", {"start": v(-102, 125) * mm, "end": v(-104, 125) * mm});
            skLineSegment(sketch, "E53.83.0.0", {"start": v(-108, -125) * mm, "end": v(-108, 125) * mm});
            skLineSegment(sketch, "E53.83.0.1", {"start": v(-106, -125) * mm, "end": v(-106, 125) * mm});
            skLineSegment(sketch, "E53.83.0.2", {"start": v(-106, -125) * mm, "end": v(-108, -125) * mm});
            skLineSegment(sketch, "E53.83.0.3", {"start": v(-106, 125) * mm, "end": v(-108, 125) * mm});
            skLineSegment(sketch, "E53.84.0.0", {"start": v(-112, -125) * mm, "end": v(-112, 125) * mm});
            skLineSegment(sketch, "E53.84.0.1", {"start": v(-110, -125) * mm, "end": v(-110, 125) * mm});
            skLineSegment(sketch, "E53.84.0.2", {"start": v(-110, -125) * mm, "end": v(-112, -125) * mm});
            skLineSegment(sketch, "E53.84.0.3", {"start": v(-110, 125) * mm, "end": v(-112, 125) * mm});
            skLineSegment(sketch, "E53.direction1", {"start": v(224, -125) * mm, "end": v(220, -125) * mm, "construction": true});
            skSolve(sketch);
        }
        {
            var Q0;
            Q0 = qSketchRegion(id + "F17", true);
            var Q1;
            Q1 = qConstructionFilter(qBodyType(qCreatedBy(id + "F17" ,EDGE), BodyType.WIRE), ConstructionObject.NO);
            extrude(context, id + "F18", {"entities" : qUnion([Q0]), "operationType" : NewBodyOperationType.REMOVE, "surfaceEntities" : qUnion([Q1]), "oppositeDirection" : true, "depth" : 0.01 * mm, "offsetDistance" : 25 * mm});
        }
        {
            var Q0;
            Q0=makeQuery(id+"F12.boolean.opBoolean","COPY",FACE,{"derivedFrom":makeQuery(id+"F12.opExtrude","CAP_FACE",FACE,{"disambiguationData":[OSD([sQuery(id+"F11.wireOp",EDGE,"E48")])],"isStart":false})});
            var sketch = newSketch(context, id + "F19", { "sketchPlane" : qUnion([Q0])});
            skLineSegment(sketch, "E54.bottom", {"start": v(28.12, 94.88) * mm, "end": v(87.88, 94.88) * mm, "construction": true});
            skLineSegment(sketch, "E54.top", {"start": v(28.12, 35.12) * mm, "end": v(87.88, 35.12) * mm, "construction": true});
            skLineSegment(sketch, "E54.left", {"start": v(28.12, 94.88) * mm, "end": v(28.12, 35.12) * mm, "construction": true});
            skLineSegment(sketch, "E54.right", {"start": v(87.88, 94.88) * mm, "end": v(87.88, 35.12) * mm, "construction": true});
            skPoint(sketch, "E54.middle", {"position": v(58, 65) * mm});
            skCircle(sketch, "E55", {"center": v(28.12, 94.88) * mm, "radius": 2.5 * mm});
            skCircle(sketch, "E56", {"center": v(87.88, 94.88) * mm, "radius": 2.5 * mm});
            skCircle(sketch, "E57", {"center": v(28.12, 35.12) * mm, "radius": 2.5 * mm});
            skCircle(sketch, "E58", {"center": v(87.88, 35.12) * mm, "radius": 2.5 * mm});
            skSolve(sketch);
        }
        {
            var Q0;
            Q0 = qSketchRegion(id + "F19", true);
            extrude(context, id + "F20", {"entities" : qUnion([Q0]), "operationType" : NewBodyOperationType.REMOVE, "oppositeDirection" : true, "depth" : 8 * mm, "offsetDistance" : 25 * mm});
        }
        {
            var Q0;
            Q0=makeQuery(id+"F6.boolean.opBoolean","COPY",FACE,{"derivedFrom":makeQuery(id+"F6.opExtrude","CAP_FACE",FACE,{"disambiguationData":[OSD([sQuery(id+"F5.wireOp",EDGE,"E45")])],"isStart":false})});
            var sketch = newSketch(context, id + "F21", { "sketchPlane" : qUnion([Q0])});
            skLineSegment(sketch, "E59.bottom", {"start": v(-51.27, -81.27) * mm, "end": v(51.27, -81.27) * mm, "construction": true});
            skLineSegment(sketch, "E59.top", {"start": v(-51.27, 21.27) * mm, "end": v(51.27, 21.27) * mm, "construction": true});
            skLineSegment(sketch, "E59.left", {"start": v(-51.27, -81.27) * mm, "end": v(-51.27, 21.27) * mm, "construction": true});
            skLineSegment(sketch, "E59.right", {"start": v(51.27, -81.27) * mm, "end": v(51.27, 21.27) * mm, "construction": true});
            skPoint(sketch, "E59.middle", {"position": v(0, -30) * mm});
            skCircle(sketch, "E60", {"center": v(-51.27, 21.27) * mm, "radius": 2.5 * mm});
            skCircle(sketch, "E61", {"center": v(51.27, 21.27) * mm, "radius": 2.5 * mm});
            skCircle(sketch, "E62", {"center": v(51.27, -81.27) * mm, "radius": 2.5 * mm});
            skCircle(sketch, "E63", {"center": v(-51.27, -81.27) * mm, "radius": 2.5 * mm});
            skSolve(sketch);
        }
        {
            var Q0;
            Q0 = qSketchRegion(id + "F21", true);
            extrude(context, id + "F22", {"entities" : qUnion([Q0]), "operationType" : NewBodyOperationType.REMOVE, "oppositeDirection" : true, "depth" : 8 * mm, "offsetDistance" : 25 * mm});
        }
        {
            var Q0;
            Q0=qCreatedBy(makeId("Top.planeOp"),FACE);
            var sketch = newSketch(context, id + "F23", { "sketchPlane" : qUnion([Q0])});
            skLineSegment(sketch, "E64.bottom", {"start": v(-273.27, 0) * mm, "end": v(-328.27, 0) * mm});
            skLineSegment(sketch, "E64.top", {"start": v(-273.27, 12.5) * mm, "end": v(-328.27, 12.5) * mm});
            skLineSegment(sketch, "E64.left", {"start": v(-273.27, 0) * mm, "end": v(-273.27, 12.5) * mm});
            skLineSegment(sketch, "E64.right", {"start": v(-328.27, 0) * mm, "end": v(-328.27, 12.5) * mm});
            skSolve(sketch);
        }
        {
            var Q0;
            Q0 = qSketchRegion(id + "F23", true);
            var Q1;
            Q1=sQuery(id+"F23.wireOp",EDGE,"E64.bottom");
            revolve(context, id + "F24", {"entities" : qUnion([Q0]), "axis" : qUnion([Q1]), "revolveType" : RevolveType.FULL});
        }
        {
            var Q0;
            Q0=qCreatedBy(makeId("Front.planeOp"),FACE);
            var sketch = newSketch(context, id + "F25", { "sketchPlane" : qUnion([Q0])});
            skCircle(sketch, "E65", {"center": v(-200, 0) * mm, "radius": 37.5 * mm});
            skSolve(sketch);
        }
        {
            var Q0;
            Q0 = qSketchRegion(id + "F25", true);
            extrude(context, id + "F26", {"entities" : qUnion([Q0]), "depth" : 22 * mm, "offsetDistance" : 25 * mm});
        }
        {
            var Q0;
            Q0=makeQuery(id+"F26.opExtrude","CAP_FACE",FACE,{"disambiguationData":[OSD([sQuery(id+"F25.wireOp",EDGE,"E65")])],"isStart":false});
            var sketch = newSketch(context, id + "F27", { "sketchPlane" : qUnion([Q0])});
            skCircle(sketch, "E66", {"center": v(-200, 0) * mm, "radius": 24.5 * mm});
            skCircle(sketch, "E67", {"center": v(-200, 0) * mm, "radius": 37.5 * mm});
            skSolve(sketch);
        }
        {
            var Q0;
            Q0 = qSketchRegion(id + "F27", true);
            extrude(context, id + "F28", {"entities" : qUnion([Q0]), "operationType" : NewBodyOperationType.REMOVE, "oppositeDirection" : true, "depth" : 19 * mm, "offsetDistance" : 25 * mm});
        }
        {
            var Q0;
            Q0=qCreatedBy(makeId("Top.planeOp"),FACE);
            var sketch = newSketch(context, id + "F29", { "sketchPlane" : qUnion([Q0])});
            skLineSegment(sketch, "E68.bottom", {"start": v(-420.19, -5) * mm, "end": v(-365.19, -5) * mm});
            skLineSegment(sketch, "E68.top", {"start": v(-420.19, 5) * mm, "end": v(-365.19, 5) * mm});
            skLineSegment(sketch, "E68.left", {"start": v(-420.19, -5) * mm, "end": v(-420.19, 5) * mm});
            skLineSegment(sketch, "E68.right", {"start": v(-365.19, -5) * mm, "end": v(-365.19, 5) * mm});
            skPoint(sketch, "E68.middle", {"position": v(-392.69, 0) * mm});
            skSolve(sketch);
        }
        {
            var Q0;
            Q0 = qSketchRegion(id + "F29", true);
            extrude(context, id + "F30", {"entities" : qUnion([Q0]), "depth" : 10 * mm, "offsetDistance" : 25 * mm});
        }
        {
            var Q0;
            Q0=makeQuery(id+"F2.opExtrude","SWEPT_FACE",FACE,{"disambiguationData":[OSD([sQuery(id+"F1.wireOp",EDGE,"E30")])]});
            var sketch = newSketch(context, id + "F31", { "sketchPlane" : qUnion([Q0])});
            skCircle(sketch, "E69", {"center": v(-58, -80) * mm, "radius": 37.5 * mm});
            skPoint(sketch, "E69.centerSnap0", {"position": v(-58, -135) * mm});
            skSolve(sketch);
        }
        {
            var Q0;
            Q0 = qSketchRegion(id + "F31", true);
            extrude(context, id + "F32", {"entities" : qUnion([Q0]), "operationType" : NewBodyOperationType.REMOVE, "oppositeDirection" : true, "depth" : 3 * mm, "offsetDistance" : 25 * mm});
        }
        {
            var Q0;
            Q0=makeQuery(id+"F32.boolean.opBoolean","COPY",FACE,{"derivedFrom":makeQuery(id+"F32.opExtrude","CAP_FACE",FACE,{"disambiguationData":[OSD([sQuery(id+"F31.wireOp",EDGE,"E69")])],"isStart":false})});
            var sketch = newSketch(context, id + "F33", { "sketchPlane" : qUnion([Q0])});
            skCircle(sketch, "E70", {"center": v(-58, -80) * mm, "radius": 25 * mm});
            skSolve(sketch);
        }
        {
            var Q0;
            Q0 = qSketchRegion(id + "F33", true);
            extrude(context, id + "F34", {"entities" : qUnion([Q0]), "operationType" : NewBodyOperationType.REMOVE, "oppositeDirection" : true, "depth" : 7 * mm, "offsetDistance" : 25 * mm});
        }
        {
            var Q0;
            Q0=makeQuery(id+"F26.opExtrude","CAP_FACE",FACE,{"disambiguationData":[OSD([sQuery(id+"F25.wireOp",EDGE,"E65")])],"isStart":true});
            var sketch = newSketch(context, id + "F35", { "sketchPlane" : qUnion([Q0])});
            skCircle(sketch, "E71", {"center": v(192, 2) * mm, "radius": 5 * mm});
            skCircle(sketch, "E72", {"center": v(208, 2) * mm, "radius": 5 * mm});
            skLineSegment(sketch, "E73", {"start": v(178.97, -8) * mm, "end": v(221.03, -8) * mm});
            skArc(sketch, "E74", {"start": v(178.97, -8) * mm, "mid": v(200, 22.5) * mm, "end": v(221.03, -8) * mm});
            skSolve(sketch);
        }
        {
            var Q0;
            Q0 = qSketchRegion(id + "F35", true);
            extrude(context, id + "F36", {"entities" : qUnion([Q0]), "operationType" : NewBodyOperationType.REMOVE, "oppositeDirection" : true, "depth" : 20 * mm, "offsetDistance" : 25 * mm});
        }
        {
            var Q0;
            Q0=makeQuery(id+"F30.opExtrude","SWEPT_FACE",FACE,{"disambiguationData":[OSD([sQuery(id+"F29.wireOp",EDGE,"E68.bottom")])]});
            var sketch = newSketch(context, id + "F37", { "sketchPlane" : qUnion([Q0])});
            skLineSegment(sketch, "E75.bottom", {"start": v(-393.19, -2.5) * mm, "end": v(-392.19, -2.5) * mm});
            skLineSegment(sketch, "E75.top", {"start": v(-393.19, 12.5) * mm, "end": v(-392.19, 12.5) * mm});
            skLineSegment(sketch, "E75.left", {"start": v(-393.19, -2.5) * mm, "end": v(-393.19, 12.5) * mm});
            skLineSegment(sketch, "E75.right", {"start": v(-392.19, -2.5) * mm, "end": v(-392.19, 12.5) * mm});
            skPoint(sketch, "E75.middle", {"position": v(-392.69, 5) * mm});
            skPoint(sketch, "E75.middle.positionSnap0", {"position": v(-420.19, 5) * mm});
            skPoint(sketch, "E75.middle.positionSnap1", {"position": v(-392.69, 10) * mm});
            skPoint(sketch, "E75.centerSnap0", {"position": v(-420.19, 5) * mm});
            skPoint(sketch, "E75.centerSnap1", {"position": v(-392.69, 10) * mm});
            skSolve(sketch);
        }
        {
            var Q0;
            Q0 = qSketchRegion(id + "F37", true);
            extrude(context, id + "F38", {"entities" : qUnion([Q0]), "operationType" : NewBodyOperationType.REMOVE, "oppositeDirection" : true, "depth" : 25 * mm, "offsetDistance" : 25 * mm});
        }
        {
            var Q0;
            Q0=qCreatedBy(makeId("Right.planeOp"),FACE);
            cPlane(context, id + "F39", {"entities" : qUnion([Q0]), "cplaneType" : CPlaneType.OFFSET, "offset" : 200 * mm, "oppositeDirection" : true, "width" : 150 * mm, "height" : 150 * mm});
        }
        {
            var Q0;
            Q0=qCreatedBy(id+"F39.planeOp",FACE);
            var sketch = newSketch(context, id + "F40", { "sketchPlane" : qUnion([Q0])});
            skLineSegment(sketch, "E76", {"start": v(-3, -24.5) * mm, "end": v(-22.16, -7.55) * mm});
            skLineSegment(sketch, "E77", {"start": v(-22.16, -7.55) * mm, "end": v(-25.46, -7.55) * mm});
            skLineSegment(sketch, "E78", {"start": v(-25.46, -7.55) * mm, "end": v(-25.46, -26.6) * mm});
            skLineSegment(sketch, "E79", {"start": v(-25.46, -26.6) * mm, "end": v(-3, -26.6) * mm});
            skLineSegment(sketch, "E80", {"start": v(-3, -26.6) * mm, "end": v(-3, -24.5) * mm});
            skSolve(sketch);
        }
        {
            var Q0;
            Q0 = qSketchRegion(id + "F40", true);
            extrude(context, id + "F41", {"entities" : qUnion([Q0]), "operationType" : NewBodyOperationType.REMOVE, "oppositeDirection" : true, "depth" : 50 * mm, "offsetDistance" : 25 * mm, "symmetric" : true});
        }
        {
            var Q0;
            Q0=qCreatedBy(id+"F39.planeOp",FACE);
            var sketch = newSketch(context, id + "F42", { "sketchPlane" : qUnion([Q0])});
            skLineSegment(sketch, "E81", {"start": v(30, 70) * mm, "end": v(-30, 70) * mm, "construction": true});
            skSolve(sketch);
        }
        {
            var Q0;
            Q0=qCreatedBy(id+"F39.planeOp",FACE);
            var sketch = newSketch(context, id + "F43", { "sketchPlane" : qUnion([Q0])});
            skPoint(sketch, "E82.middle", {"position": v(0, 70) * mm});
            skLineSegment(sketch, "E83", {"start": v(15, 57.5) * mm, "end": v(12, 57.5) * mm});
            skLineSegment(sketch, "E84", {"start": v(12, 57.5) * mm, "end": v(12, 60.5) * mm});
            skLineSegment(sketch, "E85", {"start": v(-15, 57.5) * mm, "end": v(-12, 57.5) * mm});
            skLineSegment(sketch, "E86", {"start": v(-12, 57.5) * mm, "end": v(-12, 60.5) * mm});
            skArc(sketch, "E87", {"start": v(10, 60.5) * mm, "mid": v(11, 59.5) * mm, "end": v(12, 60.5) * mm});
            skArc(sketch, "E88.1.0.0", {"start": v(8, 60.5) * mm, "mid": v(9, 59.5) * mm, "end": v(10, 60.5) * mm});
            skArc(sketch, "E88.2.0.0", {"start": v(6, 60.5) * mm, "mid": v(7, 59.5) * mm, "end": v(8, 60.5) * mm});
            skArc(sketch, "E88.3.0.0", {"start": v(4, 60.5) * mm, "mid": v(5, 59.5) * mm, "end": v(6, 60.5) * mm});
            skArc(sketch, "E88.4.0.0", {"start": v(2, 60.5) * mm, "mid": v(3, 59.5) * mm, "end": v(4, 60.5) * mm});
            skArc(sketch, "E88.5.0.0", {"start": v(0, 60.5) * mm, "mid": v(1, 59.5) * mm, "end": v(2, 60.5) * mm});
            skArc(sketch, "E88.6.0.0", {"start": v(-2, 60.5) * mm, "mid": v(-1, 59.5) * mm, "end": v(0, 60.5) * mm});
            skArc(sketch, "E88.7.0.0", {"start": v(-4, 60.5) * mm, "mid": v(-3, 59.5) * mm, "end": v(-2, 60.5) * mm});
            skArc(sketch, "E88.8.0.0", {"start": v(-6, 60.5) * mm, "mid": v(-5, 59.5) * mm, "end": v(-4, 60.5) * mm});
            skArc(sketch, "E88.9.0.0", {"start": v(-8, 60.5) * mm, "mid": v(-7, 59.5) * mm, "end": v(-6, 60.5) * mm});
            skArc(sketch, "E88.10.0.0", {"start": v(-10, 60.5) * mm, "mid": v(-9, 59.5) * mm, "end": v(-8, 60.5) * mm});
            skArc(sketch, "E88.11.0.0", {"start": v(-12, 60.5) * mm, "mid": v(-11, 59.5) * mm, "end": v(-10, 60.5) * mm});
            skLineSegment(sketch, "E88.direction1", {"start": v(10, 60.5) * mm, "end": v(8, 60.5) * mm, "construction": true});
            skLineSegment(sketch, "E89", {"start": v(15, 57.5) * mm, "end": v(15, 70) * mm});
            skLineSegment(sketch, "E90", {"start": v(15, 70) * mm, "end": v(-15, 70) * mm});
            skLineSegment(sketch, "E91", {"start": v(-15, 70) * mm, "end": v(-15, 57.5) * mm});
            skSolve(sketch);
        }
        {
            var Q0;
            Q0 = qSketchRegion(id + "F43", true);
            var Q1;
            Q1=sQuery(id+"F42.wireOp",EDGE,"E81");
            revolve(context, id + "F44", {"surfaceOperationType" : NewSurfaceOperationType.NEW, "entities" : qUnion([Q0]), "axis" : qUnion([Q1]), "revolveType" : RevolveType.FULL});
        }
    });
